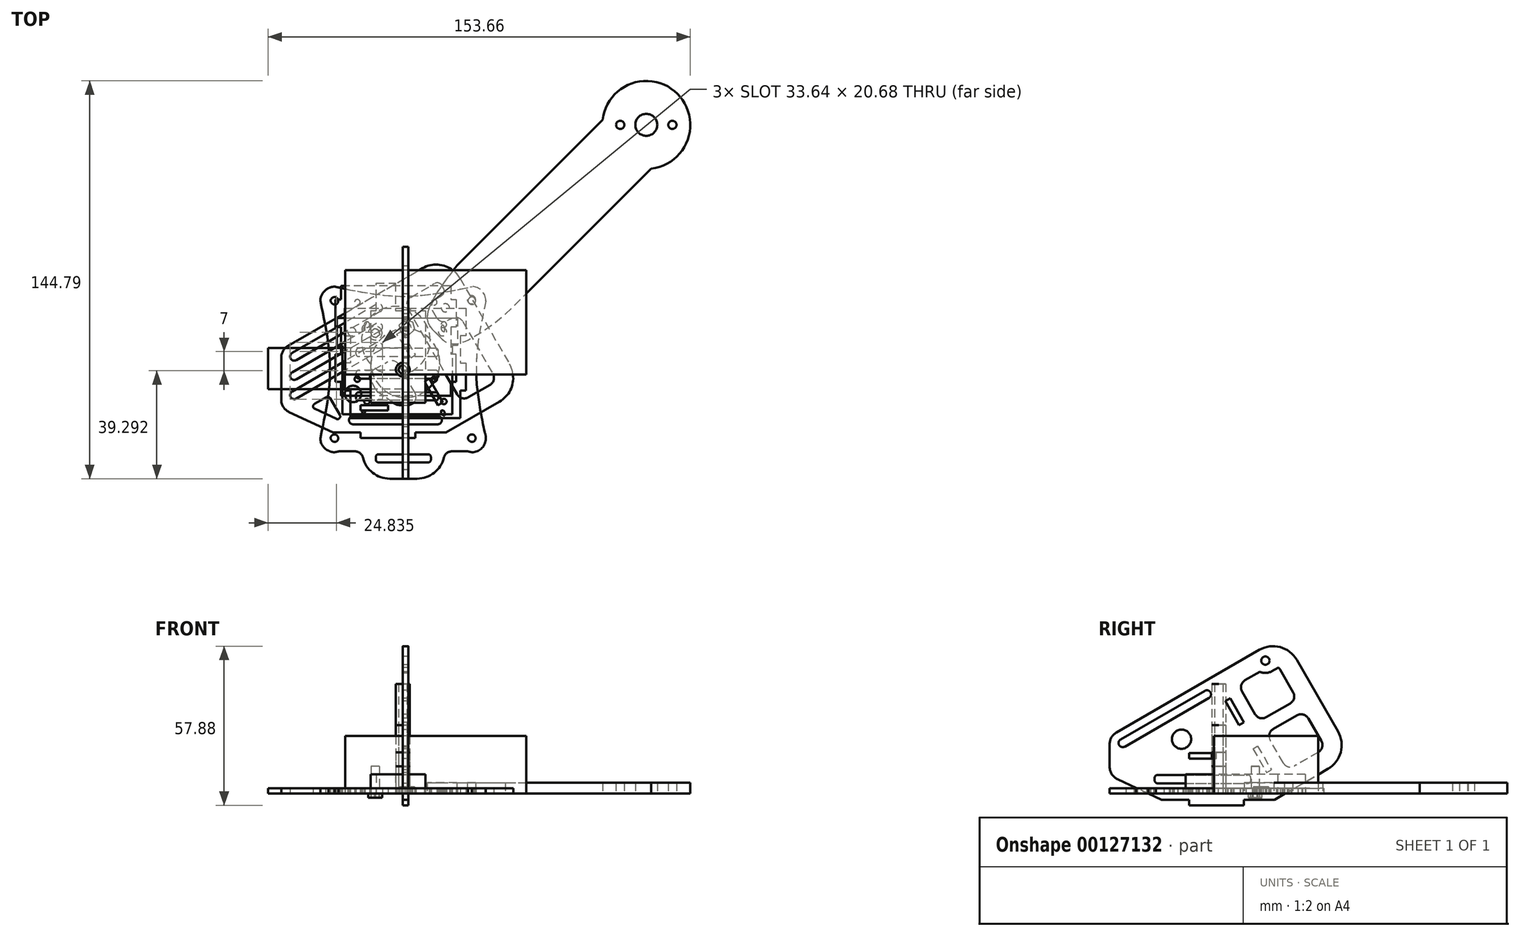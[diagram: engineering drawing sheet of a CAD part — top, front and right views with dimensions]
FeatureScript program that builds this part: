
annotation { "Feature Type Name" : "Feature", "Feature Type Description" : "" }
export const myFeature = defineFeature(function(context is Context, id is Id, definition is map)
    precondition{}
    {
        {
            var Q0;
            Q0=qCreatedBy(makeId("Top.planeOp"),FACE);
            var sketch = newSketch(context, id + "F0", { "sketchPlane" : qUnion([Q0])});
            skLineSegment(sketch, "E0.bottom", {"start": v(15.25, -15.25) * mm, "end": v(-15.25, -15.25) * mm, "construction": true});
            skLineSegment(sketch, "E0.top", {"start": v(15.25, 15.25) * mm, "end": v(-15.25, 15.25) * mm, "construction": true});
            skLineSegment(sketch, "E0.left", {"start": v(15.25, -15.25) * mm, "end": v(15.25, 15.25) * mm, "construction": true});
            skLineSegment(sketch, "E0.right", {"start": v(-15.25, -15.25) * mm, "end": v(-15.25, 15.25) * mm, "construction": true});
            skPoint(sketch, "E0.middle", {"position": v(0, 0) * mm});
            skCircle(sketch, "E1", {"center": v(-15.25, 15.25) * mm, "radius": 1.5 * mm});
            skCircle(sketch, "E2", {"center": v(15.25, 15.25) * mm, "radius": 1.5 * mm});
            skCircle(sketch, "E3", {"center": v(15.25, -15.25) * mm, "radius": 1.5 * mm});
            skCircle(sketch, "E4", {"center": v(-15.25, -15.25) * mm, "radius": 1.5 * mm});
            skLineSegment(sketch, "E5.bottom", {"start": v(18, -18) * mm, "end": v(-18, -18) * mm, "construction": true});
            skLineSegment(sketch, "E5.top", {"start": v(18, 18) * mm, "end": v(-18, 18) * mm, "construction": true});
            skLineSegment(sketch, "E5.left", {"start": v(18, -18) * mm, "end": v(18, 18) * mm, "construction": true});
            skLineSegment(sketch, "E5.right", {"start": v(-18, -18) * mm, "end": v(-18, 18) * mm, "construction": true});
            skLineSegment(sketch, "E6.bottom", {"start": v(25, -25) * mm, "end": v(-25, -25) * mm, "construction": true});
            skLineSegment(sketch, "E6.top", {"start": v(25, 25) * mm, "end": v(-25, 25) * mm, "construction": true});
            skLineSegment(sketch, "E6.left", {"start": v(25, -25) * mm, "end": v(25, 25) * mm, "construction": true});
            skLineSegment(sketch, "E6.right", {"start": v(-25, -25) * mm, "end": v(-25, 25) * mm, "construction": true});
            skCircle(sketch, "E7", {"center": v(-25, 25) * mm, "radius": 1.5 * mm});
            skCircle(sketch, "E8", {"center": v(25, 25) * mm, "radius": 1.5 * mm});
            skCircle(sketch, "E9", {"center": v(25, -25) * mm, "radius": 1.5 * mm});
            skCircle(sketch, "E10", {"center": v(-25, -25) * mm, "radius": 1.5 * mm});
            skLineSegment(sketch, "E11.bottom", {"start": v(12.5, -12.5) * mm, "end": v(-12.5, -12.5) * mm, "construction": true});
            skLineSegment(sketch, "E11.top", {"start": v(12.5, 12.5) * mm, "end": v(-12.5, 12.5) * mm, "construction": true});
            skLineSegment(sketch, "E11.left", {"start": v(12.5, -12.5) * mm, "end": v(12.5, 12.5) * mm, "construction": true});
            skLineSegment(sketch, "E11.right", {"start": v(-12.5, -12.5) * mm, "end": v(-12.5, 12.5) * mm, "construction": true});
            skArc(sketch, "E12", {"start": v(-15.25, 11.36) * mm, "mid": v(-12.5, 12.5) * mm, "end": v(-11.36, 15.25) * mm});
            skArc(sketch, "E13", {"start": v(15.25, -11.36) * mm, "mid": v(12.5, -12.5) * mm, "end": v(11.36, -15.25) * mm});
            skArc(sketch, "E14", {"start": v(-11.36, -15.25) * mm, "mid": v(-12.5, -12.5) * mm, "end": v(-15.25, -11.36) * mm});
            skLineSegment(sketch, "E15", {"start": v(-15.25, 11.36) * mm, "end": v(-15.25, -11.36) * mm});
            skLineSegment(sketch, "E16", {"start": v(-11.36, 15.25) * mm, "end": v(11.36, 15.25) * mm});
            skLineSegment(sketch, "E17", {"start": v(15.25, 11.36) * mm, "end": v(15.25, -11.36) * mm});
            skLineSegment(sketch, "E18", {"start": v(11.36, -15.25) * mm, "end": v(-11.36, -15.25) * mm});
            skArc(sketch, "E19.trimOffspring", {"start": v(11.36, 15.25) * mm, "mid": v(12.5, 12.5) * mm, "end": v(15.25, 11.36) * mm});
            skPoint(sketch, "E20.visualSharp", {"position": v(30, 30) * mm});
            skArc(sketch, "E20.filletArc", {"start": v(30, 25) * mm, "mid": v(28.54, 28.54) * mm, "end": v(25, 30) * mm});
            skPoint(sketch, "E21.visualSharp", {"position": v(-30, 30) * mm});
            skArc(sketch, "E21.filletArc", {"start": v(-25, 30) * mm, "mid": v(-28.54, 28.54) * mm, "end": v(-30, 25) * mm});
            skPoint(sketch, "E22.visualSharp", {"position": v(-30, -30) * mm});
            skArc(sketch, "E22.filletArc", {"start": v(-30, -25) * mm, "mid": v(-28.54, -28.54) * mm, "end": v(-25, -30) * mm});
            skPoint(sketch, "E23.visualSharp", {"position": v(30, -30) * mm});
            skArc(sketch, "E23.filletArc", {"start": v(25, -30) * mm, "mid": v(28.54, -28.54) * mm, "end": v(30, -25) * mm});
            skLineSegment(sketch, "E24", {"start": v(-26.5, 25) * mm, "end": v(-26.5, -25) * mm, "construction": true});
            skFitSpline(sketch, "E25", {"points": [v(-30, 25) * mm, v(-26.5, 0) * mm, v(-30, -25) * mm], "startDerivative": vector(10.5, -50) * mm, "endDerivative": vector(-10.5, -50) * mm});
            skLineSegment(sketch, "E26", {"start": v(-25, 26.5) * mm, "end": v(25, 26.5) * mm, "construction": true});
            skLineSegment(sketch, "E27", {"start": v(26.5, 25) * mm, "end": v(26.5, -25) * mm, "construction": true});
            skLineSegment(sketch, "E28", {"start": v(24.94, -26.5) * mm, "end": v(-25, -26.5) * mm, "construction": true});
            skFitSpline(sketch, "E29", {"points": [v(-25, 30) * mm, v(0, 26.5) * mm, v(25, 30) * mm], "startDerivative": vector(50, -10.5) * mm, "endDerivative": vector(50, 10.5) * mm});
            skFitSpline(sketch, "E30", {"points": [v(30, 25) * mm, v(26.5, 0) * mm, v(30, -25) * mm], "startDerivative": vector(-10.5, -50) * mm, "endDerivative": vector(10.5, -50) * mm});
            skPoint(sketch, "E31.1.internal.snap0", {"position": v(0, -25) * mm});
            skFitSpline(sketch, "E31", {"points": [v(-25, -30) * mm, v(0, -26.5) * mm, v(25, -30) * mm], "startDerivative": vector(50, 10.5) * mm, "endDerivative": vector(50, -10.5) * mm});
            skSolve(sketch);
        }
        {
            var Q0;
            Q0=makeQuery(id+"F0.imprint","IMPRINT",FACE,{"disambiguationData":[TD([[makeQuery(id+"F0.imprint","IMPRINT",EDGE,{"derivedFrom":sQuery(id+"F0.wireOp",EDGE,"E1")}),-1.0]])]});
            extrude(context, id + "F1", {"entities" : qUnion([Q0]), "depth" : 2 * mm});
        }
        {
            var Q0;
            Q0=qCreatedBy(makeId("Top.planeOp"),FACE);
            var sketch = newSketch(context, id + "F2", { "sketchPlane" : qUnion([Q0])});
            skCircle(sketch, "E32", {"center": v(0, 0) * mm, "radius": 2.5 * mm});
            skCircle(sketch, "E33", {"center": v(0, 0) * mm, "radius": 1.5 * mm});
            skSolve(sketch);
        }
        {
            var Q0;
            Q0 = qSketchRegion(id + "F2", true);
            extrude(context, id + "F3", {"entities" : qUnion([Q0]), "depth" : 25 * mm});
        }
        {
            var Q0;
            Q0=qCreatedBy(makeId("Top.planeOp"),FACE);
            var sketch = newSketch(context, id + "F4", { "sketchPlane" : qUnion([Q0])});
            skLineSegment(sketch, "E34.bottom", {"start": v(18, -18) * mm, "end": v(-18, -18) * mm});
            skLineSegment(sketch, "E34.top", {"start": v(18, 18) * mm, "end": v(-18, 18) * mm});
            skLineSegment(sketch, "E34.left", {"start": v(18, -18) * mm, "end": v(18, 18) * mm});
            skLineSegment(sketch, "E34.right", {"start": v(-18, -18) * mm, "end": v(-18, 18) * mm});
            skPoint(sketch, "E34.middle", {"position": v(0, 0) * mm});
            skLineSegment(sketch, "E35.bottom", {"start": v(-15.25, 15.25) * mm, "end": v(15.25, 15.25) * mm, "construction": true});
            skLineSegment(sketch, "E35.top", {"start": v(-15.25, -15.25) * mm, "end": v(15.25, -15.25) * mm, "construction": true});
            skLineSegment(sketch, "E35.left", {"start": v(-15.25, 15.25) * mm, "end": v(-15.25, -15.25) * mm, "construction": true});
            skLineSegment(sketch, "E35.right", {"start": v(15.25, 15.25) * mm, "end": v(15.25, -15.25) * mm, "construction": true});
            skCircle(sketch, "E36", {"center": v(-15.25, -15.25) * mm, "radius": 1.5 * mm});
            skCircle(sketch, "E37", {"center": v(-15.25, 15.25) * mm, "radius": 1.5 * mm});
            skCircle(sketch, "E38", {"center": v(15.25, 15.25) * mm, "radius": 1.5 * mm});
            skCircle(sketch, "E39", {"center": v(15.25, -15.25) * mm, "radius": 1.5 * mm});
            skSolve(sketch);
        }
        {
            var Q0;
            Q0 = qSketchRegion(id + "F4", true);
            extrude(context, id + "F5", {"entities" : qUnion([Q0]), "depth" : 2 * mm});
        }
        {
            var Q0;
            Q0=qCreatedBy(makeId("Top.planeOp"),FACE);
            var sketch = newSketch(context, id + "F6", { "sketchPlane" : qUnion([Q0])});
            skArc(sketch, "E40", {"start": v(16.31, 14.64) * mm, "mid": v(16.31, 16.76) * mm, "end": v(14.19, 16.76) * mm});
            skCircle(sketch, "E41", {"center": v(25, 25.45) * mm, "radius": 1.5 * mm});
            skPoint(sketch, "E42.visualSharp", {"position": v(30, 30.45) * mm});
            skLineSegment(sketch, "E43", {"start": v(15.25, 15.7) * mm, "end": v(25, 25.45) * mm, "construction": true});
            skLineSegment(sketch, "E44", {"start": v(28.54, 28.98) * mm, "end": v(88.64, 89.09) * mm, "construction": true});
            skCircle(sketch, "E45", {"center": v(88.64, 89.09) * mm, "radius": 13.75 * mm, "construction": true});
            skLineSegment(sketch, "E46.0", {"start": v(37.37, 20.14) * mm, "end": v(90.42, 73.18) * mm});
            skLineSegment(sketch, "E47.0", {"start": v(19.7, 37.82) * mm, "end": v(72.74, 90.86) * mm});
            skLineSegment(sketch, "E48", {"start": v(88.64, 89.09) * mm, "end": v(105.7, 106.14) * mm, "construction": true});
            skLineSegment(sketch, "E49", {"start": v(88.64, 89.09) * mm, "end": v(88.64, 75.34) * mm, "construction": true});
            skLineSegment(sketch, "E50", {"start": v(88.64, 89.09) * mm, "end": v(74.9, 89.09) * mm, "construction": true});
            skCircle(sketch, "E51", {"center": v(88.64, 89.09) * mm, "radius": 8 * mm, "construction": true});
            skCircle(sketch, "E52", {"center": v(88.64, 89.09) * mm, "radius": 9.5 * mm, "construction": true});
            skLineSegment(sketch, "E53", {"start": v(88.64, 89.09) * mm, "end": v(98.14, 89.09) * mm, "construction": true});
            skLineSegment(sketch, "E54", {"start": v(88.64, 89.09) * mm, "end": v(88.64, 98.59) * mm, "construction": true});
            skCircle(sketch, "E55", {"center": v(88.64, 81.09) * mm, "radius": 1.5 * mm, "construction": true});
            skCircle(sketch, "E56", {"center": v(79.14, 89.09) * mm, "radius": 1.5 * mm});
            skCircle(sketch, "E57", {"center": v(88.64, 97.09) * mm, "radius": 1.5 * mm, "construction": true});
            skCircle(sketch, "E58", {"center": v(98.14, 89.09) * mm, "radius": 1.5 * mm});
            skArc(sketch, "E59", {"start": v(90.42, 73.18) * mm, "mid": v(99.95, 100.4) * mm, "end": v(72.74, 90.86) * mm});
            skFitSpline(sketch, "E60", {"points": [v(19.7, 37.82) * mm, v(12.5, 12.95) * mm, v(37.37, 20.14) * mm], "startDerivative": vector(-93.64, -114.86) * mm, "endDerivative": vector(114.86, 93.64) * mm});
            skCircle(sketch, "E61", {"center": v(88.64, 89.09) * mm, "radius": 4 * mm});
            skLineSegment(sketch, "E62", {"start": v(11.16, 11.6) * mm, "end": v(21.63, 1.14) * mm, "construction": true});
            skLineSegment(sketch, "E63", {"start": v(11.16, 11.6) * mm, "end": v(-2.43, 25.2) * mm, "construction": true});
            skCircle(sketch, "E64", {"center": v(11.16, 11.6) * mm, "radius": 10 * mm, "construction": true});
            skLineSegment(sketch, "E65", {"start": v(15.25, 15.7) * mm, "end": v(18.25, 12.7) * mm, "construction": true});
            skLineSegment(sketch, "E66", {"start": v(15.25, 15.7) * mm, "end": v(12.88, 18.07) * mm, "construction": true});
            skLineSegment(sketch, "E67", {"start": v(14.19, 16.76) * mm, "end": v(11.42, 13.99) * mm});
            skLineSegment(sketch, "E68", {"start": v(16.31, 14.64) * mm, "end": v(13.54, 11.87) * mm});
            skFitSpline(sketch, "E69.trimOffspring", {"points": [v(19.7, 37.82) * mm, v(12.5, 12.95) * mm, v(37.37, 20.14) * mm], "startDerivative": vector(-93.64, -114.86) * mm, "endDerivative": vector(114.86, 93.64) * mm});
            skSolve(sketch);
        }
        {
            var Q0;
            Q0 = qSketchRegion(id + "F6", true);
            extrude(context, id + "F7", {"entities" : qUnion([Q0]), "depth" : 4 * mm});
        }
        {
            var Q0;
            Q0=qCreatedBy(makeId("Top.planeOp"),FACE);
            var sketch = newSketch(context, id + "F8", { "sketchPlane" : qUnion([Q0])});
            skPoint(sketch, "E70.visualSharp", {"position": v(30.19, 29.9) * mm});
            skArc(sketch, "E70.filletArc", {"start": v(30.19, 24.9) * mm, "mid": v(28.72, 28.44) * mm, "end": v(25.19, 29.9) * mm});
            skPoint(sketch, "E71.visualSharp", {"position": v(-29.81, 29.9) * mm});
            skArc(sketch, "E71.filletArc", {"start": v(-24.81, 29.9) * mm, "mid": v(-28.35, 28.44) * mm, "end": v(-29.81, 24.9) * mm});
            skPoint(sketch, "E72.visualSharp", {"position": v(-29.81, -30.1) * mm});
            skArc(sketch, "E72.filletArc", {"start": v(-29.81, -25.1) * mm, "mid": v(-28.35, -28.63) * mm, "end": v(-24.81, -30.1) * mm});
            skPoint(sketch, "E73.visualSharp", {"position": v(30.19, -30.1) * mm});
            skArc(sketch, "E73.filletArc", {"start": v(25.19, -30.1) * mm, "mid": v(28.72, -28.63) * mm, "end": v(30.19, -25.1) * mm});
            skFitSpline(sketch, "E74", {"points": [v(-29.81, 24.9) * mm, v(-26.31, -0.1) * mm, v(-29.81, -25.1) * mm], "startDerivative": vector(10.5, -50) * mm, "endDerivative": vector(-10.5, -50) * mm});
            skFitSpline(sketch, "E75", {"points": [v(-24.81, 29.9) * mm, v(0.19, 26.4) * mm, v(25.19, 29.9) * mm], "startDerivative": vector(50, -10.5) * mm, "endDerivative": vector(50, 10.5) * mm});
            skFitSpline(sketch, "E76", {"points": [v(30.19, 24.9) * mm, v(26.69, -0.1) * mm, v(30.19, -25.1) * mm], "startDerivative": vector(-10.5, -50) * mm, "endDerivative": vector(10.5, -50) * mm});
            skFitSpline(sketch, "E77", {"points": [v(-24.81, -30.1) * mm, v(0.19, -26.6) * mm, v(25.19, -30.1) * mm], "startDerivative": vector(50, 10.5) * mm, "endDerivative": vector(50, -10.5) * mm});
            skLineSegment(sketch, "E78", {"start": v(0.19, 26.4) * mm, "end": v(0.19, -26.6) * mm, "construction": true});
            skLineSegment(sketch, "E79", {"start": v(-26.31, -0.1) * mm, "end": v(26.69, -0.1) * mm, "construction": true});
            skCircle(sketch, "E80", {"center": v(-24.81, -25.1) * mm, "radius": 1.5 * mm});
            skCircle(sketch, "E81", {"center": v(25.19, -25.1) * mm, "radius": 1.5 * mm});
            skCircle(sketch, "E82", {"center": v(25.19, 24.9) * mm, "radius": 1.5 * mm});
            skCircle(sketch, "E83", {"center": v(-24.81, 24.9) * mm, "radius": 1.5 * mm});
            skLineSegment(sketch, "E84.left", {"start": v(17.7, -12.58) * mm, "end": v(17.68, 12.4) * mm, "construction": true});
            skPoint(sketch, "E84.middle", {"position": v(0.19, -0.1) * mm});
            skCircle(sketch, "E85", {"center": v(-15.06, 15.16) * mm, "radius": 1.5 * mm});
            skCircle(sketch, "E86", {"center": v(15.44, 15.16) * mm, "radius": 1.5 * mm});
            skCircle(sketch, "E87", {"center": v(15.44, -15.34) * mm, "radius": 1.5 * mm});
            skCircle(sketch, "E88", {"center": v(-15.06, -15.34) * mm, "radius": 1.5 * mm});
            skLineSegment(sketch, "E89.0", {"start": v(20.7, -12.58) * mm, "end": v(20.68, 12.4) * mm, "construction": true});
            skArc(sketch, "E90", {"start": v(20.68, 12.4) * mm, "mid": v(19.18, 13.9) * mm, "end": v(17.68, 12.4) * mm, "construction": true});
            skArc(sketch, "E91", {"start": v(17.7, -12.58) * mm, "mid": v(19.2, -14.08) * mm, "end": v(20.7, -12.58) * mm, "construction": true});
            skLineSegment(sketch, "E92.bottom", {"start": v(8.07, -10.1) * mm, "end": v(-7.7, -10.1) * mm});
            skLineSegment(sketch, "E92.top", {"start": v(8.07, 9.9) * mm, "end": v(-7.7, 9.9) * mm});
            skLineSegment(sketch, "E92.left", {"start": v(10.19, -7.97) * mm, "end": v(10.19, 7.79) * mm});
            skLineSegment(sketch, "E92.right", {"start": v(-9.81, -7.97) * mm, "end": v(-9.81, 7.79) * mm});
            skLineSegment(sketch, "E93", {"start": v(0.19, -0.1) * mm, "end": v(10.19, 9.9) * mm, "construction": true});
            skArc(sketch, "E94.MirrorCS", {"start": v(-12.31, -20.59) * mm, "mid": v(-13.81, -19.09) * mm, "end": v(-12.31, -17.59) * mm, "construction": true});
            skLineSegment(sketch, "E95.MirrorCS", {"start": v(-12.31, -20.59) * mm, "end": v(12.68, -20.6) * mm, "construction": true});
            skArc(sketch, "E96.MirrorCS", {"start": v(12.68, -17.6) * mm, "mid": v(14.18, -19.1) * mm, "end": v(12.68, -20.6) * mm, "construction": true});
            skLineSegment(sketch, "E97.MirrorCS", {"start": v(-12.31, -17.59) * mm, "end": v(12.68, -17.6) * mm, "construction": true});
            skArc(sketch, "E98.MirrorCS", {"start": v(-12.3, 17.41) * mm, "mid": v(-13.8, 18.91) * mm, "end": v(-12.3, 20.41) * mm, "construction": true});
            skLineSegment(sketch, "E99.MirrorCS", {"start": v(-12.3, 20.41) * mm, "end": v(12.7, 20.4) * mm, "construction": true});
            skLineSegment(sketch, "E100.MirrorCS", {"start": v(-12.3, 17.41) * mm, "end": v(12.69, 17.4) * mm, "construction": true});
            skArc(sketch, "E101.MirrorCS", {"start": v(12.7, 20.4) * mm, "mid": v(14.2, 18.9) * mm, "end": v(12.69, 17.4) * mm, "construction": true});
            skLineSegment(sketch, "E102.bottom", {"start": v(0.57, 2.4) * mm, "end": v(-0.2, 2.4) * mm});
            skLineSegment(sketch, "E102.top", {"start": v(0.57, -2.6) * mm, "end": v(-0.2, -2.6) * mm});
            skLineSegment(sketch, "E102.left", {"start": v(2.69, 0.29) * mm, "end": v(2.69, -0.47) * mm});
            skLineSegment(sketch, "E102.right", {"start": v(-2.31, 0.29) * mm, "end": v(-2.31, -0.47) * mm});
            skLineSegment(sketch, "E103.0", {"start": v(2.69, 0.29) * mm, "end": v(10.19, 7.79) * mm});
            skLineSegment(sketch, "E104.0", {"start": v(0.57, 2.4) * mm, "end": v(8.07, 9.9) * mm});
            skLineSegment(sketch, "E105.MirrorCS", {"start": v(0.57, -2.6) * mm, "end": v(8.07, -10.1) * mm});
            skLineSegment(sketch, "E106.MirrorCS", {"start": v(2.69, -0.47) * mm, "end": v(10.19, -7.97) * mm});
            skLineSegment(sketch, "E107.MirrorCS", {"start": v(-0.2, 2.4) * mm, "end": v(-7.7, 9.9) * mm});
            skLineSegment(sketch, "E108.MirrorCS", {"start": v(-2.31, 0.29) * mm, "end": v(-9.81, 7.79) * mm});
            skLineSegment(sketch, "E109.MirrorCS", {"start": v(-2.31, -0.47) * mm, "end": v(-9.81, -7.97) * mm});
            skLineSegment(sketch, "E110.MirrorCS", {"start": v(-0.2, -2.6) * mm, "end": v(-7.7, -10.1) * mm});
            skLineSegment(sketch, "E111", {"start": v(20.69, -0.1) * mm, "end": v(20.68, 9.9) * mm});
            skLineSegment(sketch, "E112", {"start": v(20.68, 9.9) * mm, "end": v(17.68, 9.9) * mm, "construction": true});
            skArc(sketch, "E113", {"start": v(20.69, 8.07) * mm, "mid": v(19.3, 9.9) * mm, "end": v(17.69, 8.28) * mm});
            skPoint(sketch, "E113.first.point", {"position": v(17.69, 8.5) * mm});
            skPoint(sketch, "E113.second.point", {"position": v(19.18, 9.9) * mm});
            skPoint(sketch, "E113.third.point", {"position": v(20.69, 8.07) * mm});
            skLineSegment(sketch, "E114.MirrorCS", {"start": v(20.68, -10.1) * mm, "end": v(17.68, -10.1) * mm, "construction": true});
            skArc(sketch, "E115.MirrorCS", {"start": v(20.69, -8.26) * mm, "mid": v(19.3, -10.09) * mm, "end": v(17.69, -8.47) * mm});
            skLineSegment(sketch, "E116", {"start": v(20.69, -0.1) * mm, "end": v(20.69, -8.26) * mm});
            skLineSegment(sketch, "E117", {"start": v(17.69, 8.28) * mm, "end": v(17.69, -8.47) * mm});
            skLineSegment(sketch, "E118.MirrorCS", {"start": v(-17.3, 8.28) * mm, "end": v(-17.3, -8.47) * mm});
            skLineSegment(sketch, "E119.MirrorCS", {"start": v(-20.31, -0.1) * mm, "end": v(-20.3, 9.9) * mm});
            skPoint(sketch, "E120.MirrorP", {"position": v(-20.3, 8.07) * mm});
            skLineSegment(sketch, "E121.MirrorCS", {"start": v(-17.32, -12.58) * mm, "end": v(-17.3, 12.4) * mm, "construction": true});
            skArc(sketch, "E122.MirrorCS", {"start": v(-20.3, 8.07) * mm, "mid": v(-18.93, 9.9) * mm, "end": v(-17.3, 8.28) * mm});
            skLineSegment(sketch, "E123.MirrorCS", {"start": v(-20.3, 9.9) * mm, "end": v(-17.3, 9.9) * mm, "construction": true});
            skPoint(sketch, "E124.MirrorP", {"position": v(-18.8, 9.9) * mm});
            skArc(sketch, "E125.MirrorCS", {"start": v(-20.3, 12.4) * mm, "mid": v(-18.8, 13.9) * mm, "end": v(-17.3, 12.4) * mm, "construction": true});
            skPoint(sketch, "E126.MirrorP", {"position": v(-17.3, 8.5) * mm});
            skLineSegment(sketch, "E127.MirrorCS", {"start": v(-20.32, -12.58) * mm, "end": v(-20.3, 12.4) * mm, "construction": true});
            skArc(sketch, "E128.MirrorCS", {"start": v(-17.32, -12.58) * mm, "mid": v(-18.82, -14.08) * mm, "end": v(-20.32, -12.58) * mm, "construction": true});
            skArc(sketch, "E129.MirrorCS", {"start": v(-20.3, -8.26) * mm, "mid": v(-18.93, -10.09) * mm, "end": v(-17.3, -8.47) * mm});
            skLineSegment(sketch, "E130.MirrorCS", {"start": v(-20.31, -0.1) * mm, "end": v(-20.3, -8.26) * mm});
            skLineSegment(sketch, "E131.MirrorCS", {"start": v(-20.3, -10.1) * mm, "end": v(-17.3, -10.1) * mm, "construction": true});
            skSolve(sketch);
        }
        {
            var Q0;
            Q0 = qSketchRegion(id + "F8", true);
            extrude(context, id + "F9", {"entities" : qUnion([Q0]), "depth" : 2 * mm});
        }
        {
            var Q0;
            Q0=qCreatedBy(makeId("Top.planeOp"),FACE);
            var sketch = newSketch(context, id + "F10", { "sketchPlane" : qUnion([Q0])});
            skPoint(sketch, "E132.visualSharp", {"position": v(30.23, 30.2) * mm});
            skArc(sketch, "E132.filletArc", {"start": v(30.23, 25.2) * mm, "mid": v(28.76, 28.73) * mm, "end": v(25.23, 30.2) * mm});
            skPoint(sketch, "E133.visualSharp", {"position": v(-29.77, 30.2) * mm});
            skArc(sketch, "E133.filletArc", {"start": v(-24.77, 30.2) * mm, "mid": v(-28.3, 28.73) * mm, "end": v(-29.77, 25.2) * mm});
            skPoint(sketch, "E134.visualSharp", {"position": v(-29.77, -29.8) * mm});
            skPoint(sketch, "E135.visualSharp", {"position": v(30.23, -29.8) * mm});
            skFitSpline(sketch, "E136", {"points": [v(-29.77, 25.2) * mm, v(-26.27, 0.2) * mm, v(-29.77, -24.8) * mm], "startDerivative": vector(10.5, -50) * mm, "endDerivative": vector(-10.5, -50) * mm});
            skFitSpline(sketch, "E137", {"points": [v(-24.77, 30.2) * mm, v(0.23, 26.7) * mm, v(25.23, 30.2) * mm], "startDerivative": vector(50, -10.5) * mm, "endDerivative": vector(50, 10.5) * mm});
            skFitSpline(sketch, "E138", {"points": [v(30.23, 25.2) * mm, v(26.73, 0.2) * mm, v(30.23, -24.8) * mm], "startDerivative": vector(-10.5, -50) * mm, "endDerivative": vector(10.5, -50) * mm});
            skCircle(sketch, "E139", {"center": v(-24.77, 25.2) * mm, "radius": 1.5 * mm});
            skCircle(sketch, "E140", {"center": v(25.23, 25.2) * mm, "radius": 1.5 * mm});
            skCircle(sketch, "E141", {"center": v(25.23, -24.8) * mm, "radius": 1.5 * mm});
            skCircle(sketch, "E142", {"center": v(-24.77, -24.8) * mm, "radius": 1.5 * mm});
            skLineSegment(sketch, "E143.top", {"start": v(5.23, -39.7) * mm, "end": v(-4.77, -39.7) * mm});
            skPoint(sketch, "E143.middle", {"position": v(0.23, -34.7) * mm});
            skArc(sketch, "E144.filletArc", {"start": v(-14.49, -32.06) * mm, "mid": v(-10.95, -37.56) * mm, "end": v(-4.77, -39.7) * mm});
            skLineSegment(sketch, "E145", {"start": v(-25.17, -29.79) * mm, "end": v(-17.4, -29.77) * mm});
            skArc(sketch, "E146.filletArc", {"start": v(-14.49, -32.06) * mm, "mid": v(-15.55, -30.41) * mm, "end": v(-17.4, -29.77) * mm});
            skArc(sketch, "E147", {"start": v(24.8, -29.79) * mm, "mid": v(29.3, -27.72) * mm, "end": v(29.8, -22.8) * mm});
            skArc(sketch, "E148", {"start": v(-29.35, -22.8) * mm, "mid": v(-28.84, -27.72) * mm, "end": v(-24.35, -29.79) * mm});
            skArc(sketch, "E149.MirrorCS", {"start": v(14.94, -32.06) * mm, "mid": v(11.4, -37.56) * mm, "end": v(5.23, -39.7) * mm});
            skLineSegment(sketch, "E150.MirrorCS", {"start": v(25.63, -29.79) * mm, "end": v(17.87, -29.77) * mm});
            skArc(sketch, "E151.MirrorCS", {"start": v(14.94, -32.06) * mm, "mid": v(16, -30.41) * mm, "end": v(17.87, -29.77) * mm});
            skLineSegment(sketch, "E152.left", {"start": v(20.23, -9.8) * mm, "end": v(20.23, 10.2) * mm});
            skLineSegment(sketch, "E152.right", {"start": v(-19.77, -9.8) * mm, "end": v(-19.77, 10.2) * mm});
            skPoint(sketch, "E152.middle", {"position": v(0.23, 0.2) * mm});
            skLineSegment(sketch, "E153.0", {"start": v(-21.77, -9.8) * mm, "end": v(-21.77, 10.2) * mm});
            skLineSegment(sketch, "E154.0", {"start": v(22.23, -9.8) * mm, "end": v(22.23, 10.2) * mm});
            skLineSegment(sketch, "E155", {"start": v(-21.77, 10.2) * mm, "end": v(-19.77, 10.2) * mm});
            skLineSegment(sketch, "E156", {"start": v(20.23, 10.2) * mm, "end": v(22.23, 10.2) * mm});
            skLineSegment(sketch, "E157", {"start": v(22.23, -9.8) * mm, "end": v(20.23, -9.8) * mm});
            skLineSegment(sketch, "E158", {"start": v(-19.77, -9.8) * mm, "end": v(-21.77, -9.8) * mm});
            skLineSegment(sketch, "E159", {"start": v(-19.77, -9.8) * mm, "end": v(-19.77, -4.8) * mm, "construction": true});
            skLineSegment(sketch, "E160", {"start": v(20.23, -4.8) * mm, "end": v(16.73, -4.8) * mm, "construction": true});
            skCircle(sketch, "E161", {"center": v(16.73, -4.8) * mm, "radius": 1.5 * mm});
            skCircle(sketch, "E162.MirrorC", {"center": v(-16.27, -4.8) * mm, "radius": 1.5 * mm});
            skLineSegment(sketch, "E163", {"start": v(-19.77, -4.8) * mm, "end": v(16.73, -4.8) * mm, "construction": true});
            skLineSegment(sketch, "E164.bottom", {"start": v(5.73, -9.8) * mm, "end": v(-5.27, -9.8) * mm});
            skLineSegment(sketch, "E164.top", {"start": v(5.73, 0.2) * mm, "end": v(-5.27, 0.2) * mm});
            skLineSegment(sketch, "E164.left", {"start": v(7.73, -7.8) * mm, "end": v(7.73, -1.8) * mm});
            skLineSegment(sketch, "E164.right", {"start": v(-7.27, -7.8) * mm, "end": v(-7.27, -1.8) * mm});
            skPoint(sketch, "E164.middle", {"position": v(0.23, -4.8) * mm});
            skPoint(sketch, "E165.visualSharp", {"position": v(-7.27, -9.8) * mm});
            skArc(sketch, "E165.filletArc", {"start": v(-7.27, -7.8) * mm, "mid": v(-6.69, -9.22) * mm, "end": v(-5.27, -9.8) * mm});
            skPoint(sketch, "E166.visualSharp", {"position": v(7.73, -9.8) * mm});
            skArc(sketch, "E166.filletArc", {"start": v(5.73, -9.8) * mm, "mid": v(7.14, -9.22) * mm, "end": v(7.73, -7.8) * mm});
            skPoint(sketch, "E167.visualSharp", {"position": v(7.73, 0.2) * mm});
            skArc(sketch, "E167.filletArc", {"start": v(7.73, -1.8) * mm, "mid": v(7.14, -0.4) * mm, "end": v(5.73, 0.2) * mm});
            skPoint(sketch, "E168.visualSharp", {"position": v(-7.27, 0.2) * mm});
            skArc(sketch, "E168.filletArc", {"start": v(-5.27, 0.2) * mm, "mid": v(-6.69, -0.4) * mm, "end": v(-7.27, -1.8) * mm});
            skLineSegment(sketch, "E169", {"start": v(0.23, 0.2) * mm, "end": v(0.23, 5.2) * mm, "construction": true});
            skLineSegment(sketch, "E170", {"start": v(0.23, 5.2) * mm, "end": v(0.23, 8.2) * mm, "construction": true});
            skLineSegment(sketch, "E171", {"start": v(0.23, 8.2) * mm, "end": v(0.23, 13.2) * mm, "construction": true});
            skLineSegment(sketch, "E172", {"start": v(0.23, 13.2) * mm, "end": v(0.23, 16.2) * mm, "construction": true});
            skLineSegment(sketch, "E173", {"start": v(0.23, -9.8) * mm, "end": v(0.23, -14.8) * mm, "construction": true});
            skLineSegment(sketch, "E174", {"start": v(0.23, -14.8) * mm, "end": v(0.23, -17.8) * mm, "construction": true});
            skLineSegment(sketch, "E175", {"start": v(0.23, -17.8) * mm, "end": v(0.23, -22.8) * mm, "construction": true});
            skLineSegment(sketch, "E176", {"start": v(0.23, -22.8) * mm, "end": v(0.23, -25.8) * mm, "construction": true});
            skLineSegment(sketch, "E177.bottom", {"start": v(14.23, -17.8) * mm, "end": v(-13.77, -17.8) * mm});
            skLineSegment(sketch, "E177.top", {"start": v(14.23, -14.8) * mm, "end": v(-13.77, -14.8) * mm});
            skLineSegment(sketch, "E177.left", {"start": v(15.23, -16.8) * mm, "end": v(15.23, -15.8) * mm});
            skLineSegment(sketch, "E177.right", {"start": v(-14.77, -16.8) * mm, "end": v(-14.77, -15.8) * mm});
            skPoint(sketch, "E177.middle", {"position": v(0.23, -16.3) * mm});
            skLineSegment(sketch, "E178.bottom", {"start": v(14.23, -25.8) * mm, "end": v(-13.77, -25.8) * mm});
            skLineSegment(sketch, "E178.top", {"start": v(14.23, -22.8) * mm, "end": v(-13.77, -22.8) * mm});
            skLineSegment(sketch, "E178.left", {"start": v(15.23, -24.8) * mm, "end": v(15.23, -23.8) * mm});
            skLineSegment(sketch, "E178.right", {"start": v(-14.77, -24.8) * mm, "end": v(-14.77, -23.8) * mm});
            skPoint(sketch, "E178.middle", {"position": v(0.23, -24.3) * mm});
            skLineSegment(sketch, "E179.bottom", {"start": v(14.23, 5.2) * mm, "end": v(-13.77, 5.2) * mm});
            skLineSegment(sketch, "E179.top", {"start": v(14.23, 8.2) * mm, "end": v(-13.77, 8.2) * mm});
            skLineSegment(sketch, "E179.left", {"start": v(15.23, 6.2) * mm, "end": v(15.23, 7.2) * mm});
            skLineSegment(sketch, "E179.right", {"start": v(-14.77, 6.2) * mm, "end": v(-14.77, 7.2) * mm});
            skPoint(sketch, "E179.middle", {"position": v(0.23, 6.7) * mm});
            skLineSegment(sketch, "E180.bottom", {"start": v(14.23, 13.2) * mm, "end": v(-13.77, 13.2) * mm});
            skLineSegment(sketch, "E180.top", {"start": v(14.23, 16.2) * mm, "end": v(-13.77, 16.2) * mm});
            skLineSegment(sketch, "E180.left", {"start": v(15.23, 14.2) * mm, "end": v(15.23, 15.2) * mm});
            skLineSegment(sketch, "E180.right", {"start": v(-14.77, 14.2) * mm, "end": v(-14.77, 15.2) * mm});
            skPoint(sketch, "E180.middle", {"position": v(0.23, 14.7) * mm});
            skPoint(sketch, "E181.visualSharp", {"position": v(-14.77, -25.8) * mm});
            skArc(sketch, "E181.filletArc", {"start": v(-14.77, -24.8) * mm, "mid": v(-14.48, -25.51) * mm, "end": v(-13.77, -25.8) * mm});
            skPoint(sketch, "E182.visualSharp", {"position": v(-14.77, -22.8) * mm});
            skArc(sketch, "E182.filletArc", {"start": v(-13.77, -22.8) * mm, "mid": v(-14.48, -23.1) * mm, "end": v(-14.77, -23.8) * mm});
            skPoint(sketch, "E183.visualSharp", {"position": v(15.23, -22.8) * mm});
            skArc(sketch, "E183.filletArc", {"start": v(15.23, -23.8) * mm, "mid": v(14.94, -23.1) * mm, "end": v(14.23, -22.8) * mm});
            skPoint(sketch, "E184.visualSharp", {"position": v(15.23, -25.8) * mm});
            skArc(sketch, "E184.filletArc", {"start": v(14.23, -25.8) * mm, "mid": v(14.94, -25.51) * mm, "end": v(15.23, -24.8) * mm});
            skPoint(sketch, "E185.visualSharp", {"position": v(-14.77, -14.8) * mm});
            skArc(sketch, "E185.filletArc", {"start": v(-13.77, -14.8) * mm, "mid": v(-14.48, -15.1) * mm, "end": v(-14.77, -15.8) * mm});
            skPoint(sketch, "E186.visualSharp", {"position": v(-14.77, -17.8) * mm});
            skArc(sketch, "E186.filletArc", {"start": v(-14.77, -16.8) * mm, "mid": v(-14.48, -17.51) * mm, "end": v(-13.77, -17.8) * mm});
            skPoint(sketch, "E187.visualSharp", {"position": v(15.23, -14.8) * mm});
            skArc(sketch, "E187.filletArc", {"start": v(15.23, -15.8) * mm, "mid": v(14.94, -15.1) * mm, "end": v(14.23, -14.8) * mm});
            skPoint(sketch, "E188.visualSharp", {"position": v(15.23, -17.8) * mm});
            skArc(sketch, "E188.filletArc", {"start": v(14.23, -17.8) * mm, "mid": v(14.94, -17.51) * mm, "end": v(15.23, -16.8) * mm});
            skPoint(sketch, "E189.visualSharp", {"position": v(15.23, 5.2) * mm});
            skArc(sketch, "E189.filletArc", {"start": v(14.23, 5.2) * mm, "mid": v(14.94, 5.49) * mm, "end": v(15.23, 6.2) * mm});
            skPoint(sketch, "E190.visualSharp", {"position": v(15.23, 8.2) * mm});
            skArc(sketch, "E190.filletArc", {"start": v(15.23, 7.2) * mm, "mid": v(14.94, 7.9) * mm, "end": v(14.23, 8.2) * mm});
            skPoint(sketch, "E191.visualSharp", {"position": v(-14.77, 8.2) * mm});
            skArc(sketch, "E191.filletArc", {"start": v(-13.77, 8.2) * mm, "mid": v(-14.48, 7.9) * mm, "end": v(-14.77, 7.2) * mm});
            skPoint(sketch, "E192.visualSharp", {"position": v(-14.77, 5.2) * mm});
            skArc(sketch, "E192.filletArc", {"start": v(-14.77, 6.2) * mm, "mid": v(-14.48, 5.49) * mm, "end": v(-13.77, 5.2) * mm});
            skPoint(sketch, "E193.visualSharp", {"position": v(-14.77, 16.2) * mm});
            skArc(sketch, "E193.filletArc", {"start": v(-13.77, 16.2) * mm, "mid": v(-14.48, 15.9) * mm, "end": v(-14.77, 15.2) * mm});
            skPoint(sketch, "E194.visualSharp", {"position": v(15.23, 16.2) * mm});
            skArc(sketch, "E194.filletArc", {"start": v(15.23, 15.2) * mm, "mid": v(14.94, 15.9) * mm, "end": v(14.23, 16.2) * mm});
            skPoint(sketch, "E195.visualSharp", {"position": v(15.23, 13.2) * mm});
            skArc(sketch, "E195.filletArc", {"start": v(14.23, 13.2) * mm, "mid": v(14.94, 13.49) * mm, "end": v(15.23, 14.2) * mm});
            skPoint(sketch, "E196.visualSharp", {"position": v(-14.77, 13.2) * mm});
            skArc(sketch, "E196.filletArc", {"start": v(-14.77, 14.2) * mm, "mid": v(-14.48, 13.49) * mm, "end": v(-13.77, 13.2) * mm});
            skLineSegment(sketch, "E197", {"start": v(0.23, 16.2) * mm, "end": v(0.23, 21.2) * mm, "construction": true});
            skLineSegment(sketch, "E198", {"start": v(0.23, 21.2) * mm, "end": v(0.23, 24.2) * mm, "construction": true});
            skLineSegment(sketch, "E199.bottom", {"start": v(14.23, 21.2) * mm, "end": v(-13.77, 21.2) * mm});
            skLineSegment(sketch, "E199.top", {"start": v(14.23, 24.2) * mm, "end": v(-13.77, 24.2) * mm});
            skLineSegment(sketch, "E199.left", {"start": v(15.23, 22.2) * mm, "end": v(15.23, 23.2) * mm});
            skLineSegment(sketch, "E199.right", {"start": v(-14.77, 22.2) * mm, "end": v(-14.77, 23.2) * mm});
            skPoint(sketch, "E199.middle", {"position": v(0.23, 22.7) * mm});
            skPoint(sketch, "E200.visualSharp", {"position": v(-14.77, 24.2) * mm});
            skArc(sketch, "E200.filletArc", {"start": v(-13.77, 24.2) * mm, "mid": v(-14.48, 23.9) * mm, "end": v(-14.77, 23.2) * mm});
            skPoint(sketch, "E201.visualSharp", {"position": v(-14.77, 21.2) * mm});
            skArc(sketch, "E201.filletArc", {"start": v(-14.77, 22.2) * mm, "mid": v(-14.48, 21.49) * mm, "end": v(-13.77, 21.2) * mm});
            skPoint(sketch, "E202.visualSharp", {"position": v(15.23, 21.2) * mm});
            skArc(sketch, "E202.filletArc", {"start": v(14.23, 21.2) * mm, "mid": v(14.94, 21.49) * mm, "end": v(15.23, 22.2) * mm});
            skPoint(sketch, "E203.visualSharp", {"position": v(15.23, 24.2) * mm});
            skArc(sketch, "E203.filletArc", {"start": v(15.23, 23.2) * mm, "mid": v(14.94, 23.9) * mm, "end": v(14.23, 24.2) * mm});
            skLineSegment(sketch, "E204", {"start": v(0.23, -25.8) * mm, "end": v(0.23, -30.8) * mm, "construction": true});
            skLineSegment(sketch, "E205", {"start": v(0.23, -30.8) * mm, "end": v(0.23, -33.8) * mm, "construction": true});
            skLineSegment(sketch, "E206.bottom", {"start": v(9.23, -33.8) * mm, "end": v(-8.77, -33.8) * mm});
            skLineSegment(sketch, "E206.top", {"start": v(9.23, -30.8) * mm, "end": v(-8.77, -30.8) * mm});
            skLineSegment(sketch, "E206.left", {"start": v(10.23, -32.8) * mm, "end": v(10.23, -31.8) * mm});
            skLineSegment(sketch, "E206.right", {"start": v(-9.77, -32.8) * mm, "end": v(-9.77, -31.8) * mm});
            skPoint(sketch, "E206.middle", {"position": v(0.23, -32.3) * mm});
            skPoint(sketch, "E207.visualSharp", {"position": v(10.23, -30.8) * mm});
            skArc(sketch, "E207.filletArc", {"start": v(10.23, -31.8) * mm, "mid": v(9.94, -31.1) * mm, "end": v(9.23, -30.8) * mm});
            skPoint(sketch, "E208.visualSharp", {"position": v(10.23, -33.8) * mm});
            skArc(sketch, "E208.filletArc", {"start": v(9.23, -33.8) * mm, "mid": v(9.94, -33.51) * mm, "end": v(10.23, -32.8) * mm});
            skPoint(sketch, "E209.visualSharp", {"position": v(-9.77, -30.8) * mm});
            skArc(sketch, "E209.filletArc", {"start": v(-8.77, -30.8) * mm, "mid": v(-9.48, -31.1) * mm, "end": v(-9.77, -31.8) * mm});
            skPoint(sketch, "E210.visualSharp", {"position": v(-9.77, -33.8) * mm});
            skArc(sketch, "E210.filletArc", {"start": v(-9.77, -32.8) * mm, "mid": v(-9.48, -33.51) * mm, "end": v(-8.77, -33.8) * mm});
            skSolve(sketch);
        }
        {
            var Q0;
            Q0=qCreatedBy(makeId("Top.planeOp"),FACE);
            var sketch = newSketch(context, id + "F11", { "sketchPlane" : qUnion([Q0])});
            skCircle(sketch, "E211", {"center": v(1.48, 15.4) * mm, "radius": 1.5 * mm});
            skLineSegment(sketch, "E212.0", {"start": v(4.25, 14.6) * mm, "end": v(2.16, 12.6) * mm});
            skLineSegment(sketch, "E212.1", {"start": v(2.16, 12.6) * mm, "end": v(-0.6, 13.4) * mm});
            skLineSegment(sketch, "E212.2", {"start": v(-0.6, 13.4) * mm, "end": v(-1.3, 16.21) * mm});
            skLineSegment(sketch, "E212.3", {"start": v(-1.3, 16.21) * mm, "end": v(0.8, 18.2) * mm});
            skLineSegment(sketch, "E212.4", {"start": v(0.8, 18.2) * mm, "end": v(3.56, 17.4) * mm});
            skLineSegment(sketch, "E212.5", {"start": v(3.56, 17.4) * mm, "end": v(4.25, 14.6) * mm});
            skPoint(sketch, "E212.0.midPoint", {"position": v(3.2, 13.6) * mm});
            skSolve(sketch);
        }
        {
            var Q0;
            Q0 = qSketchRegion(id + "F11", true);
            extrude(context, id + "F12", {"entities" : qUnion([Q0]), "depth" : 2.5 * mm});
        }
        {
            var Q0;
            Q0 = qSketchRegion(id + "F2", true);
            extrude(context, id + "F13", {"entities" : qUnion([Q0]), "depth" : 10 * mm});
        }
        {
            var Q0;
            Q0 = qSketchRegion(id + "F10", true);
            extrude(context, id + "F14", {"entities" : qUnion([Q0]), "depth" : 2 * mm});
        }
        {
            var Q0;
            Q0=qCreatedBy(makeId("Top.planeOp"),FACE);
            var sketch = newSketch(context, id + "F15", { "sketchPlane" : qUnion([Q0])});
            skCircle(sketch, "E213", {"center": v(-10.03, 13.3) * mm, "radius": 1.5 * mm});
            skCircle(sketch, "E214", {"center": v(-10.03, 13.3) * mm, "radius": 2.5 * mm});
            skCircle(sketch, "E215.cCircle", {"center": v(-10.03, 13.3) * mm, "radius": 1.5 * mm, "construction": true});
            skLineSegment(sketch, "E215.0", {"start": v(-10.26, 15.02) * mm, "end": v(-8.66, 14.36) * mm});
            skLineSegment(sketch, "E215.1", {"start": v(-8.66, 14.36) * mm, "end": v(-8.43, 12.64) * mm});
            skLineSegment(sketch, "E215.2", {"start": v(-8.43, 12.64) * mm, "end": v(-9.8, 11.58) * mm});
            skLineSegment(sketch, "E215.3", {"start": v(-9.8, 11.58) * mm, "end": v(-11.4, 12.25) * mm});
            skLineSegment(sketch, "E215.4", {"start": v(-11.4, 12.25) * mm, "end": v(-11.63, 13.97) * mm});
            skLineSegment(sketch, "E215.5", {"start": v(-11.63, 13.97) * mm, "end": v(-10.26, 15.02) * mm});
            skPoint(sketch, "E215.0.midPoint", {"position": v(-9.46, 14.69) * mm});
            skCircle(sketch, "E216", {"center": v(-10.03, 13.3) * mm, "radius": 1.73 * mm});
            skSolve(sketch);
        }
        {
            var Q0;
            {var subQ1=sQuery(id+"F15.wireOp",EDGE,"E215.0");var subQ3=makeQuery(id+"F15.imprint","INTERSECT",VERTEX,{"derivedFrom":[sQuery(id+"F15.wireOp",EDGE,"E213"),subQ1]});Q0=makeQuery(id+"F15.imprint","IMPRINT",FACE,{"disambiguationData":[TD([[makeQuery(id+"F15.imprint","IMPRINT",EDGE,{"disambiguationData":[TD([[subQ3,1.0]])],"derivedFrom":subQ1}),1.0]])]});}
            var Q1;
            {var subQ1=sQuery(id+"F15.wireOp",EDGE,"E215.5");var subQ3=makeQuery(id+"F15.imprint","INTERSECT",VERTEX,{"derivedFrom":[sQuery(id+"F15.wireOp",EDGE,"E213"),subQ1]});Q1=makeQuery(id+"F15.imprint","IMPRINT",FACE,{"disambiguationData":[TD([[makeQuery(id+"F15.imprint","IMPRINT",EDGE,{"disambiguationData":[TD([[subQ3,1.0]])],"derivedFrom":subQ1}),1.0]])]});}
            var Q2;
            {var subQ1=sQuery(id+"F15.wireOp",EDGE,"E215.4");var subQ3=makeQuery(id+"F15.imprint","INTERSECT",VERTEX,{"derivedFrom":[sQuery(id+"F15.wireOp",EDGE,"E213"),subQ1]});Q2=makeQuery(id+"F15.imprint","IMPRINT",FACE,{"disambiguationData":[TD([[makeQuery(id+"F15.imprint","IMPRINT",EDGE,{"disambiguationData":[TD([[subQ3,1.0]])],"derivedFrom":subQ1}),1.0]])]});}
            var Q3;
            {var subQ1=sQuery(id+"F15.wireOp",EDGE,"E215.3");var subQ3=makeQuery(id+"F15.imprint","INTERSECT",VERTEX,{"derivedFrom":[sQuery(id+"F15.wireOp",EDGE,"E213"),subQ1]});Q3=makeQuery(id+"F15.imprint","IMPRINT",FACE,{"disambiguationData":[TD([[makeQuery(id+"F15.imprint","IMPRINT",EDGE,{"disambiguationData":[TD([[subQ3,1.0]])],"derivedFrom":subQ1}),1.0]])]});}
            var Q4;
            {var subQ1=sQuery(id+"F15.wireOp",EDGE,"E215.2");var subQ3=makeQuery(id+"F15.imprint","INTERSECT",VERTEX,{"derivedFrom":[sQuery(id+"F15.wireOp",EDGE,"E213"),subQ1]});Q4=makeQuery(id+"F15.imprint","IMPRINT",FACE,{"disambiguationData":[TD([[makeQuery(id+"F15.imprint","IMPRINT",EDGE,{"disambiguationData":[TD([[subQ3,1.0]])],"derivedFrom":subQ1}),1.0]])]});}
            var Q5;
            {var subQ1=sQuery(id+"F15.wireOp",EDGE,"E215.1");var subQ3=makeQuery(id+"F15.imprint","INTERSECT",VERTEX,{"derivedFrom":[sQuery(id+"F15.wireOp",EDGE,"E213"),subQ1]});Q5=makeQuery(id+"F15.imprint","IMPRINT",FACE,{"disambiguationData":[TD([[makeQuery(id+"F15.imprint","IMPRINT",EDGE,{"disambiguationData":[TD([[subQ3,1.0]])],"derivedFrom":subQ1}),1.0]])]});}
            var Q6;
            Q6=makeQuery(id+"F15.imprint","IMPRINT",FACE,{"disambiguationData":[TD([[makeQuery(id+"F15.imprint","IMPRINT",EDGE,{"derivedFrom":sQuery(id+"F15.wireOp",EDGE,"E214")}),1.0]])]});
            extrude(context, id + "F16", {"entities" : qUnion([Q0, Q1, Q2, Q3, Q4, Q5, Q6]), "oppositeDirection" : true, "depth" : 3 * mm, "symmetric" : true});
        }
        {
            var Q0;
            {var subQ0=sQuery(id+"F15.wireOp",EDGE,"E215.3");var subQ1=sQuery(id+"F15.wireOp",EDGE,"E213");var subQ2=makeQuery(id+"F15.imprint","INTERSECT",VERTEX,{"derivedFrom":[subQ1,subQ0]});Q0=makeQuery(id+"F15.imprint","IMPRINT",FACE,{"disambiguationData":[TD([[makeQuery(id+"F15.imprint","IMPRINT",EDGE,{"disambiguationData":[TD([[subQ2,-1.0]])],"derivedFrom":subQ1}),-1.0]])]});}
            var Q1;
            {var subQ0=sQuery(id+"F15.wireOp",EDGE,"E215.1");var subQ1=sQuery(id+"F15.wireOp",EDGE,"E213");var subQ2=makeQuery(id+"F15.imprint","INTERSECT",VERTEX,{"derivedFrom":[subQ1,subQ0]});Q1=makeQuery(id+"F15.imprint","IMPRINT",FACE,{"disambiguationData":[TD([[makeQuery(id+"F15.imprint","IMPRINT",EDGE,{"disambiguationData":[TD([[subQ2,1.0]])],"derivedFrom":subQ1}),-1.0]])]});}
            var Q2;
            {var subQ0=sQuery(id+"F15.wireOp",EDGE,"E215.0");var subQ1=sQuery(id+"F15.wireOp",EDGE,"E213");var subQ2=makeQuery(id+"F15.imprint","INTERSECT",VERTEX,{"derivedFrom":[subQ1,subQ0]});Q2=makeQuery(id+"F15.imprint","IMPRINT",FACE,{"disambiguationData":[TD([[makeQuery(id+"F15.imprint","IMPRINT",EDGE,{"disambiguationData":[TD([[subQ2,1.0]])],"derivedFrom":subQ1}),-1.0]])]});}
            var Q3;
            {var subQ0=sQuery(id+"F15.wireOp",EDGE,"E215.0");var subQ1=sQuery(id+"F15.wireOp",EDGE,"E213");var subQ2=makeQuery(id+"F15.imprint","INTERSECT",VERTEX,{"derivedFrom":[subQ1,subQ0]});Q3=makeQuery(id+"F15.imprint","IMPRINT",FACE,{"disambiguationData":[TD([[makeQuery(id+"F15.imprint","IMPRINT",EDGE,{"disambiguationData":[TD([[subQ2,-1.0]])],"derivedFrom":subQ1}),-1.0]])]});}
            var Q4;
            {var subQ0=sQuery(id+"F15.wireOp",EDGE,"E215.5");var subQ1=sQuery(id+"F15.wireOp",EDGE,"E213");var subQ2=makeQuery(id+"F15.imprint","INTERSECT",VERTEX,{"derivedFrom":[subQ1,subQ0]});Q4=makeQuery(id+"F15.imprint","IMPRINT",FACE,{"disambiguationData":[TD([[makeQuery(id+"F15.imprint","IMPRINT",EDGE,{"disambiguationData":[TD([[subQ2,-1.0]])],"derivedFrom":subQ1}),-1.0]])]});}
            var Q5;
            {var subQ0=sQuery(id+"F15.wireOp",EDGE,"E215.4");var subQ1=sQuery(id+"F15.wireOp",EDGE,"E213");var subQ2=makeQuery(id+"F15.imprint","INTERSECT",VERTEX,{"derivedFrom":[subQ1,subQ0]});Q5=makeQuery(id+"F15.imprint","IMPRINT",FACE,{"disambiguationData":[TD([[makeQuery(id+"F15.imprint","IMPRINT",EDGE,{"disambiguationData":[TD([[subQ2,-1.0]])],"derivedFrom":subQ1}),-1.0]])]});}
            extrude(context, id + "F17", {"entities" : qUnion([Q0, Q1, Q2, Q3, Q4, Q5]), "operationType" : NewBodyOperationType.ADD, "depth" : 1.5 * mm});
        }
        {
            var Q0;
            {var subQ0=sQuery(id+"F15.wireOp",EDGE,"E213");var subQ4=makeQuery(id+"F15.imprint","INTERSECT",VERTEX,{"derivedFrom":[subQ0,sQuery(id+"F15.wireOp",EDGE,"E215.0")]});Q0=makeQuery(id+"F15.imprint","IMPRINT",FACE,{"disambiguationData":[TD([[makeQuery(id+"F15.imprint","IMPRINT",EDGE,{"disambiguationData":[TD([[subQ4,1.0]])],"derivedFrom":subQ0}),1.0]])]});}
            extrude(context, id + "F18", {"entities" : qUnion([Q0]), "operationType" : NewBodyOperationType.ADD, "depth" : 10 * mm});
        }
        {
            var Q0;
            Q0=qCreatedBy(makeId("Right.planeOp"),FACE);
            var sketch = newSketch(context, id + "F19", { "sketchPlane" : qUnion([Q0])});
            skLineSegment(sketch, "E217.bottom", {"start": v(-20.84, -2.21) * mm, "end": v(-10.82, -2.21) * mm});
            skLineSegment(sketch, "E218.top", {"start": v(9.18, -4.21) * mm, "end": v(-10.82, -4.21) * mm});
            skLineSegment(sketch, "E218.left", {"start": v(9.18, -2.21) * mm, "end": v(9.18, -4.21) * mm});
            skLineSegment(sketch, "E218.right", {"start": v(-10.82, -2.21) * mm, "end": v(-10.82, -4.21) * mm});
            skLineSegment(sketch, "E219.trimOffspring", {"start": v(9.18, -2.21) * mm, "end": v(20.29, -2.21) * mm});
            skLineSegment(sketch, "E220", {"start": v(20.29, -2.21) * mm, "end": v(39.76, 9.03) * mm});
            skLineSegment(sketch, "E221", {"start": v(-20.84, -2.21) * mm, "end": v(-36.82, 5.24) * mm});
            skLineSegment(sketch, "E222", {"start": v(-39.7, 18) * mm, "end": v(-39.7, 9.77) * mm});
            skPoint(sketch, "E223.visualSharp", {"position": v(-39.7, 20.89) * mm});
            skArc(sketch, "E223.filletArc", {"start": v(-37.2, 22.33) * mm, "mid": v(-39.03, 20.5) * mm, "end": v(-39.7, 18) * mm});
            skPoint(sketch, "E224.visualSharp", {"position": v(-39.7, 6.59) * mm});
            skArc(sketch, "E224.filletArc", {"start": v(-39.7, 9.77) * mm, "mid": v(-38.92, 7.08) * mm, "end": v(-36.82, 5.24) * mm});
            skLineSegment(sketch, "E225", {"start": v(-37.2, 22.33) * mm, "end": v(14.76, 52.33) * mm});
            skLineSegment(sketch, "E226", {"start": v(28.42, 48.67) * mm, "end": v(43.42, 22.7) * mm});
            skPoint(sketch, "E227.visualSharp", {"position": v(23.42, 57.33) * mm});
            skArc(sketch, "E227.filletArc", {"start": v(28.42, 48.67) * mm, "mid": v(22.35, 53.33) * mm, "end": v(14.76, 52.33) * mm});
            skPoint(sketch, "E228.visualSharp", {"position": v(48.42, 14.03) * mm});
            skArc(sketch, "E228.filletArc", {"start": v(39.76, 9.03) * mm, "mid": v(44.42, 15.1) * mm, "end": v(43.42, 22.7) * mm});
            skLineSegment(sketch, "E229", {"start": v(35.92, 35.68) * mm, "end": v(9.94, 20.68) * mm, "construction": true});
            skLineSegment(sketch, "E230", {"start": v(-11.22, 37.33) * mm, "end": v(-9.72, 34.73) * mm, "construction": true});
            skLineSegment(sketch, "E231", {"start": v(-5.04, 37.44) * mm, "end": v(-35.7, 19.73) * mm});
            skLineSegment(sketch, "E232.0", {"start": v(-3.54, 34.84) * mm, "end": v(-34.2, 17.14) * mm});
            skArc(sketch, "E233", {"start": v(-3.54, 34.84) * mm, "mid": v(-3, 36.89) * mm, "end": v(-5.04, 37.44) * mm});
            skArc(sketch, "E234", {"start": v(-35.7, 19.73) * mm, "mid": v(-36.25, 17.69) * mm, "end": v(-34.2, 17.14) * mm});
            skLineSegment(sketch, "E235", {"start": v(-5.04, 37.44) * mm, "end": v(16.26, 49.73) * mm, "construction": true});
            skLineSegment(sketch, "E236", {"start": v(-3.54, 34.84) * mm, "end": v(17.76, 47.14) * mm, "construction": true});
            skLineSegment(sketch, "E237", {"start": v(16.26, 49.73) * mm, "end": v(17.76, 47.14) * mm, "construction": true});
            skCircle(sketch, "E238", {"center": v(17, 48.44) * mm, "radius": 1.5 * mm});
            skLineSegment(sketch, "E239.0", {"start": v(24.17, 0.03) * mm, "end": v(-0.83, 43.33) * mm, "construction": true});
            skLineSegment(sketch, "E240", {"start": v(7.44, 25.01) * mm, "end": v(2.44, 33.67) * mm});
            skLineSegment(sketch, "E241", {"start": v(12.44, 16.35) * mm, "end": v(17.44, 7.7) * mm});
            skLineSegment(sketch, "E242.0", {"start": v(22.44, -0.97) * mm, "end": v(-2.56, 42.33) * mm, "construction": true});
            skLineSegment(sketch, "E243", {"start": v(17.44, 7.7) * mm, "end": v(19.17, 8.7) * mm});
            skLineSegment(sketch, "E244", {"start": v(12.44, 16.35) * mm, "end": v(14.17, 17.35) * mm});
            skLineSegment(sketch, "E245", {"start": v(7.44, 25.01) * mm, "end": v(9.17, 26.01) * mm});
            skLineSegment(sketch, "E246", {"start": v(2.44, 33.67) * mm, "end": v(4.17, 34.67) * mm});
            skLineSegment(sketch, "E247", {"start": v(4.17, 34.67) * mm, "end": v(9.17, 26.01) * mm});
            skLineSegment(sketch, "E248", {"start": v(14.17, 17.35) * mm, "end": v(19.17, 8.7) * mm});
            skLineSegment(sketch, "E249", {"start": v(-10.04, 22.84) * mm, "end": v(-10.04, 21.84) * mm});
            skLineSegment(sketch, "E250", {"start": v(-10.04, 21.84) * mm, "end": v(-13.54, 21.84) * mm, "construction": true});
            skCircle(sketch, "E251", {"center": v(-13.54, 21.84) * mm, "radius": 3.5 * mm, "construction": true});
            skLineSegment(sketch, "E252.0", {"start": v(22.36, 45.17) * mm, "end": v(27.1, 36.95) * mm});
            skArc(sketch, "E253.0", {"start": v(36.26, 15.1) * mm, "mid": v(37.66, 16.92) * mm, "end": v(37.36, 19.2) * mm});
            skArc(sketch, "E254.0", {"start": v(22.36, 45.17) * mm, "mid": v(20.53, 46.57) * mm, "end": v(18.26, 46.27) * mm});
            skLineSegment(sketch, "E255", {"start": v(23.5, 11.2) * mm, "end": v(18.75, 19.42) * mm});
            skLineSegment(sketch, "E256.trimOffspring", {"start": v(9.6, 41.27) * mm, "end": v(15.02, 44.4) * mm});
            skPoint(sketch, "E257.visualSharp", {"position": v(7, 39.77) * mm});
            skArc(sketch, "E257.filletArc", {"start": v(9.6, 41.27) * mm, "mid": v(8.2, 39.45) * mm, "end": v(8.5, 37.17) * mm});
            skLineSegment(sketch, "E258", {"start": v(36.26, 15.1) * mm, "end": v(27.6, 10.1) * mm});
            skPoint(sketch, "E259.visualSharp", {"position": v(25, 8.6) * mm});
            skArc(sketch, "E259.filletArc", {"start": v(23.5, 11.2) * mm, "mid": v(25.32, 9.8) * mm, "end": v(27.6, 10.1) * mm});
            skLineSegment(sketch, "E260.0", {"start": v(26, 32.85) * mm, "end": v(17.35, 27.85) * mm});
            skLineSegment(sketch, "E261.0", {"start": v(28.5, 28.52) * mm, "end": v(19.85, 23.52) * mm});
            skLineSegment(sketch, "E262.trimOffspring", {"start": v(32.6, 27.42) * mm, "end": v(37.36, 19.2) * mm});
            skLineSegment(sketch, "E263.trimOffspring", {"start": v(13.25, 28.95) * mm, "end": v(8.5, 37.17) * mm});
            skPoint(sketch, "E264.visualSharp", {"position": v(31.1, 30.02) * mm});
            skArc(sketch, "E264.filletArc", {"start": v(32.6, 27.42) * mm, "mid": v(30.78, 28.82) * mm, "end": v(28.5, 28.52) * mm});
            skPoint(sketch, "E265.visualSharp", {"position": v(17.25, 22.02) * mm});
            skArc(sketch, "E265.filletArc", {"start": v(19.85, 23.52) * mm, "mid": v(18.45, 21.7) * mm, "end": v(18.75, 19.42) * mm});
            skPoint(sketch, "E266.visualSharp", {"position": v(14.75, 26.35) * mm});
            skArc(sketch, "E266.filletArc", {"start": v(13.25, 28.95) * mm, "mid": v(15.07, 27.55) * mm, "end": v(17.35, 27.85) * mm});
            skPoint(sketch, "E267.visualSharp", {"position": v(28.6, 34.35) * mm});
            skArc(sketch, "E267.filletArc", {"start": v(26, 32.85) * mm, "mid": v(27.4, 34.67) * mm, "end": v(27.1, 36.95) * mm});
            skLineSegment(sketch, "E268", {"start": v(9.18, -2.21) * mm, "end": v(-10.82, -2.21) * mm, "construction": true});
            skLineSegment(sketch, "E269", {"start": v(-10.82, -2.21) * mm, "end": v(-5.82, -2.21) * mm});
            skLineSegment(sketch, "E270", {"start": v(-5.82, -2.21) * mm, "end": v(-5.82, 33.52) * mm, "construction": true});
            skLineSegment(sketch, "E271", {"start": v(-5.82, -2.21) * mm, "end": v(-5.82, 12.79) * mm});
            skLineSegment(sketch, "E272", {"start": v(-5.82, 12.79) * mm, "end": v(-5.82, 14.79) * mm});
            skLineSegment(sketch, "E273.bottom", {"start": v(-10.82, 12.79) * mm, "end": v(-0.82, 12.79) * mm});
            skLineSegment(sketch, "E273.top", {"start": v(-10.82, 14.79) * mm, "end": v(-0.82, 14.79) * mm});
            skLineSegment(sketch, "E273.left", {"start": v(-10.82, 12.79) * mm, "end": v(-10.82, 14.79) * mm});
            skLineSegment(sketch, "E273.right", {"start": v(-0.82, 12.79) * mm, "end": v(-0.82, 14.79) * mm});
            skPoint(sketch, "E273.middle", {"position": v(-5.82, 13.79) * mm});
            skLineSegment(sketch, "E274.bottom", {"start": v(-22.32, 3.79) * mm, "end": v(10.68, 3.79) * mm});
            skLineSegment(sketch, "E274.top", {"start": v(-22.32, 6.79) * mm, "end": v(10.68, 6.79) * mm});
            skLineSegment(sketch, "E274.left", {"start": v(-23.32, 4.79) * mm, "end": v(-23.32, 5.79) * mm});
            skLineSegment(sketch, "E274.right", {"start": v(11.68, 4.79) * mm, "end": v(11.68, 5.79) * mm});
            skPoint(sketch, "E274.middle", {"position": v(-5.82, 5.29) * mm});
            skPoint(sketch, "E275.visualSharp", {"position": v(11.68, 6.79) * mm});
            skArc(sketch, "E275.filletArc", {"start": v(11.68, 5.79) * mm, "mid": v(11.39, 6.5) * mm, "end": v(10.68, 6.79) * mm});
            skPoint(sketch, "E276.visualSharp", {"position": v(11.68, 3.79) * mm});
            skArc(sketch, "E276.filletArc", {"start": v(10.68, 3.79) * mm, "mid": v(11.39, 4.08) * mm, "end": v(11.68, 4.79) * mm});
            skPoint(sketch, "E277.visualSharp", {"position": v(-23.32, 3.79) * mm});
            skArc(sketch, "E277.filletArc", {"start": v(-23.32, 4.79) * mm, "mid": v(-23.03, 4.08) * mm, "end": v(-22.32, 3.79) * mm});
            skPoint(sketch, "E278.visualSharp", {"position": v(-23.32, 6.79) * mm});
            skArc(sketch, "E278.filletArc", {"start": v(-22.32, 6.79) * mm, "mid": v(-23.03, 6.5) * mm, "end": v(-23.32, 5.79) * mm});
            skLineSegment(sketch, "E279", {"start": v(17.76, 47.14) * mm, "end": v(19.26, 44.54) * mm, "construction": true});
            skArc(sketch, "E280", {"start": v(15.02, 44.4) * mm, "mid": v(17.16, 43.94) * mm, "end": v(19.26, 44.54) * mm});
            skLineSegment(sketch, "E281", {"start": v(19.26, 44.54) * mm, "end": v(21.7, 45.95) * mm});
            skLineSegment(sketch, "E282", {"start": v(15.02, 44.4) * mm, "end": v(18.26, 46.27) * mm, "construction": true});
            skLineSegment(sketch, "E283", {"start": v(-13.54, 21.84) * mm, "end": v(-13.54, 19.84) * mm, "construction": true});
            skCircle(sketch, "E284", {"center": v(-13.54, 19.84) * mm, "radius": 3.5 * mm});
            skSolve(sketch);
        }
        {
            var Q0;
            Q0 = qSketchRegion(id + "F19", true);
            extrude(context, id + "F20", {"entities" : qUnion([Q0]), "depth" : 2 * mm});
        }
        {
            var Q0;
            Q0 = qSketchRegion(id + "F2", true);
            extrude(context, id + "F21", {"entities" : qUnion([Q0]), "depth" : 40 * mm});
        }
        {
            var Q0;
            Q0 = qSketchRegion(id + "F2", true);
            extrude(context, id + "F22", {"entities" : qUnion([Q0]), "depth" : 15 * mm});
        }
        {
            var Q0;
            Q0=qCreatedBy(makeId("Top.planeOp"),FACE);
            var sketch = newSketch(context, id + "F23", { "sketchPlane" : qUnion([Q0])});
            skLineSegment(sketch, "E285.bottom", {"start": v(17.96, -16.25) * mm, "end": v(-22.04, -16.25) * mm});
            skLineSegment(sketch, "E285.top", {"start": v(17.96, 18.75) * mm, "end": v(-22.04, 18.75) * mm});
            skPoint(sketch, "E285.middle", {"position": v(-2.04, 1.25) * mm});
            skLineSegment(sketch, "E286", {"start": v(-22.04, -16.25) * mm, "end": v(-22.04, 8.75) * mm});
            skLineSegment(sketch, "E287", {"start": v(17.96, 8.75) * mm, "end": v(17.96, -16.25) * mm});
            skCircle(sketch, "E288", {"center": v(-18.54, 13.76) * mm, "radius": 1.5 * mm});
            skLineSegment(sketch, "E289", {"start": v(17.96, 13.76) * mm, "end": v(14.46, 13.76) * mm, "construction": true});
            skCircle(sketch, "E290", {"center": v(14.46, 13.76) * mm, "radius": 1.5 * mm});
            skLineSegment(sketch, "E291", {"start": v(-22.04, 18.75) * mm, "end": v(-24.04, 18.75) * mm});
            skLineSegment(sketch, "E292", {"start": v(-24.04, 18.75) * mm, "end": v(-24.04, 8.75) * mm});
            skLineSegment(sketch, "E293", {"start": v(-24.04, 8.75) * mm, "end": v(-22.04, 8.75) * mm});
            skLineSegment(sketch, "E294.MirrorCS", {"start": v(19.96, 18.75) * mm, "end": v(19.96, 8.75) * mm});
            skLineSegment(sketch, "E295.MirrorCS", {"start": v(19.96, 8.75) * mm, "end": v(17.96, 8.75) * mm});
            skLineSegment(sketch, "E296.MirrorCS", {"start": v(17.96, 18.75) * mm, "end": v(19.96, 18.75) * mm});
            skLineSegment(sketch, "E297", {"start": v(17.96, 8.75) * mm, "end": v(17.96, 18.75) * mm, "construction": true});
            skLineSegment(sketch, "E298", {"start": v(-22.04, 18.75) * mm, "end": v(-22.04, 8.75) * mm, "construction": true});
            skLineSegment(sketch, "E299", {"start": v(-2.04, -16.25) * mm, "end": v(-2.04, -11.25) * mm});
            skLineSegment(sketch, "E300", {"start": v(-2.04, -11.25) * mm, "end": v(-2.04, -8.25) * mm});
            skLineSegment(sketch, "E301", {"start": v(-2.04, -8.25) * mm, "end": v(-2.04, -3.25) * mm});
            skLineSegment(sketch, "E302", {"start": v(-2.04, -3.25) * mm, "end": v(-2.04, -0.25) * mm});
            skLineSegment(sketch, "E303.bottom", {"start": v(11.96, -11.25) * mm, "end": v(-16.04, -11.25) * mm});
            skLineSegment(sketch, "E303.top", {"start": v(11.96, -8.25) * mm, "end": v(-16.04, -8.25) * mm});
            skLineSegment(sketch, "E303.left", {"start": v(12.96, -10.25) * mm, "end": v(12.96, -9.25) * mm});
            skLineSegment(sketch, "E303.right", {"start": v(-17.04, -10.25) * mm, "end": v(-17.04, -9.25) * mm});
            skPoint(sketch, "E303.middle", {"position": v(-2.04, -9.75) * mm});
            skLineSegment(sketch, "E304.bottom", {"start": v(11.96, -3.25) * mm, "end": v(-16.04, -3.25) * mm});
            skLineSegment(sketch, "E304.top", {"start": v(11.96, -0.25) * mm, "end": v(-16.04, -0.25) * mm});
            skLineSegment(sketch, "E304.left", {"start": v(12.96, -2.25) * mm, "end": v(12.96, -1.25) * mm});
            skLineSegment(sketch, "E304.right", {"start": v(-17.04, -2.25) * mm, "end": v(-17.04, -1.25) * mm});
            skPoint(sketch, "E304.middle", {"position": v(-2.04, -1.75) * mm});
            skLineSegment(sketch, "E305", {"start": v(-2.04, -0.25) * mm, "end": v(-2.04, 4.75) * mm});
            skLineSegment(sketch, "E306", {"start": v(-2.04, 4.75) * mm, "end": v(-2.04, 7.75) * mm});
            skLineSegment(sketch, "E307.bottom", {"start": v(11.96, 4.75) * mm, "end": v(-16.04, 4.75) * mm});
            skLineSegment(sketch, "E307.top", {"start": v(11.96, 7.75) * mm, "end": v(-16.04, 7.75) * mm});
            skLineSegment(sketch, "E307.left", {"start": v(12.96, 5.75) * mm, "end": v(12.96, 6.75) * mm});
            skLineSegment(sketch, "E307.right", {"start": v(-17.04, 5.75) * mm, "end": v(-17.04, 6.75) * mm});
            skPoint(sketch, "E307.middle", {"position": v(-2.04, 6.25) * mm});
            skPoint(sketch, "E308.visualSharp", {"position": v(-17.04, 7.75) * mm});
            skArc(sketch, "E308.filletArc", {"start": v(-16.04, 7.75) * mm, "mid": v(-16.75, 7.46) * mm, "end": v(-17.04, 6.75) * mm});
            skPoint(sketch, "E309.visualSharp", {"position": v(-17.04, 4.75) * mm});
            skArc(sketch, "E309.filletArc", {"start": v(-17.04, 5.75) * mm, "mid": v(-16.75, 5.05) * mm, "end": v(-16.04, 4.75) * mm});
            skPoint(sketch, "E310.visualSharp", {"position": v(12.96, 4.75) * mm});
            skArc(sketch, "E310.filletArc", {"start": v(11.96, 4.75) * mm, "mid": v(12.67, 5.05) * mm, "end": v(12.96, 5.75) * mm});
            skPoint(sketch, "E311.visualSharp", {"position": v(12.96, 7.75) * mm});
            skArc(sketch, "E311.filletArc", {"start": v(12.96, 6.75) * mm, "mid": v(12.67, 7.46) * mm, "end": v(11.96, 7.75) * mm});
            skPoint(sketch, "E312.visualSharp", {"position": v(12.96, -0.25) * mm});
            skArc(sketch, "E312.filletArc", {"start": v(12.96, -1.25) * mm, "mid": v(12.67, -0.54) * mm, "end": v(11.96, -0.25) * mm});
            skPoint(sketch, "E313.visualSharp", {"position": v(12.96, -3.25) * mm});
            skArc(sketch, "E313.filletArc", {"start": v(11.96, -3.25) * mm, "mid": v(12.67, -2.95) * mm, "end": v(12.96, -2.25) * mm});
            skPoint(sketch, "E314.visualSharp", {"position": v(-17.04, -3.25) * mm});
            skArc(sketch, "E314.filletArc", {"start": v(-17.04, -2.25) * mm, "mid": v(-16.75, -2.95) * mm, "end": v(-16.04, -3.25) * mm});
            skPoint(sketch, "E315.visualSharp", {"position": v(-17.04, -0.25) * mm});
            skArc(sketch, "E315.filletArc", {"start": v(-16.04, -0.25) * mm, "mid": v(-16.75, -0.54) * mm, "end": v(-17.04, -1.25) * mm});
            skPoint(sketch, "E316.visualSharp", {"position": v(-17.04, -8.25) * mm});
            skArc(sketch, "E316.filletArc", {"start": v(-16.04, -8.25) * mm, "mid": v(-16.75, -8.54) * mm, "end": v(-17.04, -9.25) * mm});
            skPoint(sketch, "E317.visualSharp", {"position": v(12.96, -8.25) * mm});
            skArc(sketch, "E317.filletArc", {"start": v(12.96, -9.25) * mm, "mid": v(12.67, -8.54) * mm, "end": v(11.96, -8.25) * mm});
            skPoint(sketch, "E318.visualSharp", {"position": v(12.96, -11.25) * mm});
            skArc(sketch, "E318.filletArc", {"start": v(11.96, -11.25) * mm, "mid": v(12.67, -10.95) * mm, "end": v(12.96, -10.25) * mm});
            skPoint(sketch, "E319.visualSharp", {"position": v(-17.04, -11.25) * mm});
            skArc(sketch, "E319.filletArc", {"start": v(-17.04, -10.25) * mm, "mid": v(-16.75, -10.95) * mm, "end": v(-16.04, -11.25) * mm});
            skSolve(sketch);
        }
        {
            var Q0;
            Q0 = qSketchRegion(id + "F23", true);
            extrude(context, id + "F24", {"entities" : qUnion([Q0]), "depth" : 2 * mm});
        }
        {
            var Q0;
            Q0=qCreatedBy(makeId("Top.planeOp"),FACE);
            var sketch = newSketch(context, id + "F25", { "sketchPlane" : qUnion([Q0])});
            skLineSegment(sketch, "E320.bottom", {"start": v(17.46, -9.47) * mm, "end": v(-22.54, -9.47) * mm});
            skLineSegment(sketch, "E320.top", {"start": v(17.46, 30.53) * mm, "end": v(-22.54, 30.53) * mm});
            skPoint(sketch, "E320.middle", {"position": v(-2.54, 10.53) * mm});
            skLineSegment(sketch, "E321", {"start": v(17.46, 25.53) * mm, "end": v(19.46, 25.53) * mm});
            skLineSegment(sketch, "E322", {"start": v(19.46, 25.53) * mm, "end": v(19.46, 15.53) * mm});
            skLineSegment(sketch, "E323", {"start": v(19.46, 15.53) * mm, "end": v(17.46, 15.53) * mm});
            skLineSegment(sketch, "E324.MirrorCS", {"start": v(17.46, -4.47) * mm, "end": v(19.46, -4.47) * mm});
            skLineSegment(sketch, "E325.MirrorCS", {"start": v(19.46, -4.47) * mm, "end": v(19.46, 5.53) * mm});
            skLineSegment(sketch, "E326.MirrorCS", {"start": v(19.46, 5.53) * mm, "end": v(17.46, 5.53) * mm});
            skLineSegment(sketch, "E327.MirrorCS", {"start": v(-22.54, 25.53) * mm, "end": v(-24.54, 25.53) * mm});
            skLineSegment(sketch, "E328.MirrorCS", {"start": v(-24.54, 5.53) * mm, "end": v(-22.54, 5.53) * mm});
            skLineSegment(sketch, "E329.MirrorCS", {"start": v(-24.54, 15.53) * mm, "end": v(-22.54, 15.53) * mm});
            skLineSegment(sketch, "E330.MirrorCS", {"start": v(-22.54, -4.47) * mm, "end": v(-24.54, -4.47) * mm});
            skLineSegment(sketch, "E331.MirrorCS", {"start": v(-24.54, -4.47) * mm, "end": v(-24.54, 5.53) * mm});
            skLineSegment(sketch, "E332.MirrorCS", {"start": v(-24.54, 25.53) * mm, "end": v(-24.54, 15.53) * mm});
            skLineSegment(sketch, "E333", {"start": v(-22.54, 30.53) * mm, "end": v(-22.54, 25.53) * mm});
            skLineSegment(sketch, "E334", {"start": v(-22.54, 25.53) * mm, "end": v(-22.54, 15.53) * mm, "construction": true});
            skLineSegment(sketch, "E335", {"start": v(-22.54, 15.53) * mm, "end": v(-22.54, 5.53) * mm});
            skLineSegment(sketch, "E336", {"start": v(-22.54, 5.53) * mm, "end": v(-22.54, -4.47) * mm, "construction": true});
            skLineSegment(sketch, "E337", {"start": v(-22.54, -4.47) * mm, "end": v(-22.54, -9.47) * mm});
            skLineSegment(sketch, "E338", {"start": v(17.46, 30.53) * mm, "end": v(17.46, 25.53) * mm});
            skLineSegment(sketch, "E339", {"start": v(17.46, 15.53) * mm, "end": v(17.46, 5.53) * mm});
            skLineSegment(sketch, "E340", {"start": v(17.46, -4.47) * mm, "end": v(17.46, -9.47) * mm});
            skLineSegment(sketch, "E341", {"start": v(17.46, 25.53) * mm, "end": v(17.46, 15.53) * mm, "construction": true});
            skLineSegment(sketch, "E342", {"start": v(17.46, 5.53) * mm, "end": v(17.46, -4.47) * mm, "construction": true});
            skLineSegment(sketch, "E343.bottom", {"start": v(11.46, -3.47) * mm, "end": v(-16.54, -3.47) * mm, "construction": true});
            skLineSegment(sketch, "E343.top", {"start": v(11.46, 24.53) * mm, "end": v(-16.54, 24.53) * mm, "construction": true});
            skLineSegment(sketch, "E343.left", {"start": v(11.46, -3.47) * mm, "end": v(11.46, 24.53) * mm, "construction": true});
            skLineSegment(sketch, "E343.right", {"start": v(-16.54, -3.47) * mm, "end": v(-16.54, 24.53) * mm, "construction": true});
            skCircle(sketch, "E344", {"center": v(11.46, 24.53) * mm, "radius": 1 * mm});
            skCircle(sketch, "E345", {"center": v(-16.54, 24.53) * mm, "radius": 1 * mm});
            skCircle(sketch, "E346", {"center": v(11.46, -3.47) * mm, "radius": 1 * mm});
            skCircle(sketch, "E347", {"center": v(-16.54, -3.47) * mm, "radius": 1 * mm});
            skCircle(sketch, "E348", {"center": v(-2.54, 10.53) * mm, "radius": 12.5 * mm});
            skSolve(sketch);
        }
        {
            var Q0;
            Q0 = qSketchRegion(id + "F25", true);
            extrude(context, id + "F26", {"entities" : qUnion([Q0]), "depth" : 2 * mm});
        }
        {
            var Q0;
            Q0=qCreatedBy(makeId("Top.planeOp"),FACE);
            var sketch = newSketch(context, id + "F27", { "sketchPlane" : qUnion([Q0])});
            skLineSegment(sketch, "E349.bottom", {"start": v(-0.02, -7.12) * mm, "end": v(-49.02, -7.12) * mm});
            skLineSegment(sketch, "E349.top", {"start": v(-0.02, 7.88) * mm, "end": v(-49.02, 7.88) * mm});
            skLineSegment(sketch, "E349.left", {"start": v(-0.02, -7.12) * mm, "end": v(-0.02, 7.88) * mm});
            skLineSegment(sketch, "E349.right", {"start": v(-49.02, -7.12) * mm, "end": v(-49.02, 7.88) * mm});
            skPoint(sketch, "E349.middle", {"position": v(-24.52, 0.38) * mm});
            skSolve(sketch);
        }
        {
            var Q0;
            Q0 = qSketchRegion(id + "F27", true);
            extrude(context, id + "F28", {"entities" : qUnion([Q0]), "depth" : 2 * mm});
        }
        {
            var Q0;
            Q0=qCreatedBy(makeId("Top.planeOp"),FACE);
            var sketch = newSketch(context, id + "F29", { "sketchPlane" : qUnion([Q0])});
            skLineSegment(sketch, "E350.bottom", {"start": v(-11.72, 21.48) * mm, "end": v(8.28, 21.48) * mm});
            skLineSegment(sketch, "E350.top", {"start": v(-11.72, -12.02) * mm, "end": v(8.28, -12.02) * mm});
            skLineSegment(sketch, "E350.left", {"start": v(-11.72, 21.48) * mm, "end": v(-11.72, -12.02) * mm});
            skLineSegment(sketch, "E350.right", {"start": v(8.28, 21.48) * mm, "end": v(8.28, -12.02) * mm});
            skLineSegment(sketch, "E351.bottom", {"start": v(-11.72, 21.48) * mm, "end": v(-9.72, 21.48) * mm});
            skLineSegment(sketch, "E351.top", {"start": v(-11.72, 21.48) * mm, "end": v(-9.72, 21.48) * mm});
            skLineSegment(sketch, "E351.left", {"start": v(-11.72, 21.48) * mm, "end": v(-11.72, 21.48) * mm});
            skLineSegment(sketch, "E351.right", {"start": v(-9.72, 21.48) * mm, "end": v(-9.72, 21.48) * mm});
            skLineSegment(sketch, "E352", {"start": v(-9.72, 21.48) * mm, "end": v(-9.72, 31.48) * mm});
            skLineSegment(sketch, "E353", {"start": v(-9.72, 31.48) * mm, "end": v(-2.72, 31.48) * mm});
            skLineSegment(sketch, "E354", {"start": v(-2.72, 31.48) * mm, "end": v(-2.72, 21.48) * mm});
            skSolve(sketch);
        }
        {
            var Q0;
            Q0 = qSketchRegion(id + "F29", true);
            extrude(context, id + "F30", {"entities" : qUnion([Q0]), "depth" : 7 * mm});
        }
        {
            var Q0;
            Q0=qCreatedBy(makeId("Top.planeOp"),FACE);
            var sketch = newSketch(context, id + "F31", { "sketchPlane" : qUnion([Q0])});
            skLineSegment(sketch, "E355.bottom", {"start": v(-25.4, -22.9) * mm, "end": v(-15.38, -22.9) * mm});
            skLineSegment(sketch, "E356.top", {"start": v(4.62, -24.9) * mm, "end": v(-15.38, -24.9) * mm});
            skLineSegment(sketch, "E356.left", {"start": v(4.62, -22.9) * mm, "end": v(4.62, -24.9) * mm});
            skLineSegment(sketch, "E356.right", {"start": v(-15.38, -22.9) * mm, "end": v(-15.38, -24.9) * mm});
            skLineSegment(sketch, "E357.trimOffspring", {"start": v(4.62, -22.9) * mm, "end": v(15.72, -22.9) * mm});
            skLineSegment(sketch, "E358", {"start": v(15.72, -22.9) * mm, "end": v(35.2, -11.66) * mm});
            skLineSegment(sketch, "E359", {"start": v(-25.4, -22.9) * mm, "end": v(-41.38, -15.46) * mm});
            skLineSegment(sketch, "E360", {"start": v(-44.27, -2.7) * mm, "end": v(-44.27, -10.92) * mm});
            skPoint(sketch, "E361.visualSharp", {"position": v(-44.27, -14.1) * mm});
            skArc(sketch, "E361.filletArc", {"start": v(-44.27, -10.92) * mm, "mid": v(-43.48, -13.61) * mm, "end": v(-41.38, -15.46) * mm});
            skLineSegment(sketch, "E362", {"start": v(23.86, 27.98) * mm, "end": v(38.86, 2) * mm});
            skPoint(sketch, "E363.visualSharp", {"position": v(18.86, 36.64) * mm});
            skPoint(sketch, "E364.visualSharp", {"position": v(43.86, -6.66) * mm});
            skArc(sketch, "E364.filletArc", {"start": v(35.2, -11.66) * mm, "mid": v(39.86, -5.6) * mm, "end": v(38.86, 2) * mm});
            skLineSegment(sketch, "E365", {"start": v(-15.78, 16.64) * mm, "end": v(-14.28, 14.04) * mm, "construction": true});
            skLineSegment(sketch, "E366", {"start": v(-9.6, 16.74) * mm, "end": v(-40.27, -0.96) * mm});
            skLineSegment(sketch, "E367.0", {"start": v(-8.1, 14.14) * mm, "end": v(-38.77, -3.56) * mm});
            skArc(sketch, "E368", {"start": v(-8.1, 14.14) * mm, "mid": v(-7.55, 16.2) * mm, "end": v(-9.6, 16.74) * mm});
            skArc(sketch, "E369", {"start": v(-40.27, -0.96) * mm, "mid": v(-40.81, -3) * mm, "end": v(-38.77, -3.56) * mm});
            skLineSegment(sketch, "E370", {"start": v(2.88, 4.32) * mm, "end": v(-2.12, 12.98) * mm});
            skLineSegment(sketch, "E371", {"start": v(7.88, -4.34) * mm, "end": v(12.88, -13) * mm});
            skLineSegment(sketch, "E372", {"start": v(12.88, -13) * mm, "end": v(14.6, -12) * mm});
            skLineSegment(sketch, "E373", {"start": v(7.88, -4.34) * mm, "end": v(9.6, -3.34) * mm});
            skLineSegment(sketch, "E374", {"start": v(2.88, 4.32) * mm, "end": v(4.6, 5.32) * mm});
            skLineSegment(sketch, "E375", {"start": v(-2.12, 12.98) * mm, "end": v(-0.4, 13.98) * mm});
            skLineSegment(sketch, "E376", {"start": v(-0.4, 13.98) * mm, "end": v(4.6, 5.32) * mm});
            skLineSegment(sketch, "E377", {"start": v(9.6, -3.34) * mm, "end": v(14.6, -12) * mm});
            skLineSegment(sketch, "E378", {"start": v(4.62, -22.9) * mm, "end": v(-15.38, -22.9) * mm, "construction": true});
            skLineSegment(sketch, "E379", {"start": v(-15.38, -22.9) * mm, "end": v(-10.38, -22.9) * mm});
            skLineSegment(sketch, "E380.0", {"start": v(-15.38, -14.9) * mm, "end": v(-5.38, -14.9) * mm});
            skLineSegment(sketch, "E381.0", {"start": v(-15.38, -12.9) * mm, "end": v(-5.38, -12.9) * mm});
            skLineSegment(sketch, "E382", {"start": v(-5.38, -12.9) * mm, "end": v(-5.38, -14.9) * mm});
            skLineSegment(sketch, "E383", {"start": v(-15.38, -12.9) * mm, "end": v(-15.38, -14.9) * mm});
            skLineSegment(sketch, "E384", {"start": v(-8.85, 15.44) * mm, "end": v(-8.85, 8.44) * mm, "construction": true});
            skLineSegment(sketch, "E385", {"start": v(-9.6, 9.74) * mm, "end": v(-40.27, -7.96) * mm});
            skLineSegment(sketch, "E386.0", {"start": v(-8.1, 7.14) * mm, "end": v(-38.77, -10.56) * mm});
            skArc(sketch, "E387", {"start": v(-8.1, 7.14) * mm, "mid": v(-7.55, 9.2) * mm, "end": v(-9.6, 9.74) * mm});
            skArc(sketch, "E388", {"start": v(-40.27, -7.96) * mm, "mid": v(-40.81, -10) * mm, "end": v(-38.77, -10.56) * mm});
            skCircle(sketch, "E389", {"center": v(15.48, 22.5) * mm, "radius": 1.5 * mm});
            skLineSegment(sketch, "E390.0", {"start": v(21.82, 17.5) * mm, "end": v(32.8, -1.5) * mm});
            skArc(sketch, "E391.0", {"start": v(31.7, -5.6) * mm, "mid": v(33.1, -3.78) * mm, "end": v(32.8, -1.5) * mm});
            skLineSegment(sketch, "E392.0", {"start": v(23.9, -10.1) * mm, "end": v(31.7, -5.6) * mm});
            skLineSegment(sketch, "E393.0", {"start": v(7.33, 12.6) * mm, "end": v(19.8, -9) * mm});
            skPoint(sketch, "E394.visualSharp", {"position": v(21.3, -11.6) * mm});
            skArc(sketch, "E394.filletArc", {"start": v(19.8, -9) * mm, "mid": v(21.63, -10.4) * mm, "end": v(23.9, -10.1) * mm});
            skLineSegment(sketch, "E395", {"start": v(17.73, 18.6) * mm, "end": v(16.43, 17.84) * mm});
            skLineSegment(sketch, "E396", {"start": v(11.58, 20.24) * mm, "end": v(12.33, 18.94) * mm});
            skLineSegment(sketch, "E397", {"start": v(11.58, 20.24) * mm, "end": v(11.3, 20.73) * mm});
            skLineSegment(sketch, "E398", {"start": v(7.33, 12.6) * mm, "end": v(4.8, 16.98) * mm});
            skPoint(sketch, "E399.visualSharp", {"position": v(20.32, 20.1) * mm});
            skArc(sketch, "E399.filletArc", {"start": v(21.82, 17.5) * mm, "mid": v(20, 18.9) * mm, "end": v(17.73, 18.6) * mm});
            skPoint(sketch, "E400.visualSharp", {"position": v(13.83, 16.34) * mm});
            skArc(sketch, "E400.filletArc", {"start": v(12.33, 18.94) * mm, "mid": v(14.15, 17.54) * mm, "end": v(16.43, 17.84) * mm});
            skLineSegment(sketch, "E401", {"start": v(-8.85, 15.44) * mm, "end": v(-8.85, 22.44) * mm, "construction": true});
            skLineSegment(sketch, "E402", {"start": v(-9.6, 23.74) * mm, "end": v(-40.27, 6.04) * mm});
            skLineSegment(sketch, "E403.0", {"start": v(-8.1, 21.14) * mm, "end": v(-38.77, 3.44) * mm});
            skArc(sketch, "E404", {"start": v(-8.1, 21.14) * mm, "mid": v(-7.55, 23.2) * mm, "end": v(-9.6, 23.74) * mm});
            skArc(sketch, "E405", {"start": v(-40.27, 6.04) * mm, "mid": v(-40.81, 4) * mm, "end": v(-38.77, 3.44) * mm});
            skLineSegment(sketch, "E406.0", {"start": v(-11.1, 26.34) * mm, "end": v(-41.77, 8.64) * mm});
            skLineSegment(sketch, "E407", {"start": v(-44.27, -2.7) * mm, "end": v(-44.27, 4.3) * mm});
            skLineSegment(sketch, "E408", {"start": v(23.86, 27.98) * mm, "end": v(20.82, 33.23) * mm});
            skLineSegment(sketch, "E409", {"start": v(-11.1, 26.34) * mm, "end": v(7.16, 36.89) * mm});
            skArc(sketch, "E410.filletArc", {"start": v(20.82, 33.23) * mm, "mid": v(14.75, 37.89) * mm, "end": v(7.16, 36.89) * mm});
            skPoint(sketch, "E411.visualSharp", {"position": v(-44.27, 7.2) * mm});
            skArc(sketch, "E411.filletArc", {"start": v(-41.77, 8.64) * mm, "mid": v(-43.6, 6.8) * mm, "end": v(-44.27, 4.3) * mm});
            skLineSegment(sketch, "E412", {"start": v(11.58, 20.24) * mm, "end": v(10.83, 21.54) * mm});
            skLineSegment(sketch, "E413", {"start": v(13.23, 26.39) * mm, "end": v(11.93, 25.64) * mm});
            skPoint(sketch, "E414.visualSharp", {"position": v(9.33, 24.14) * mm});
            skArc(sketch, "E414.filletArc", {"start": v(11.93, 25.64) * mm, "mid": v(10.53, 23.82) * mm, "end": v(10.83, 21.54) * mm});
            skLineSegment(sketch, "E415", {"start": v(13.23, 26.39) * mm, "end": v(13.23, 26.39) * mm});
            skPoint(sketch, "E416.visualSharp", {"position": v(15.82, 27.89) * mm});
            skPoint(sketch, "E417.visualSharp", {"position": v(11.26, 35.79) * mm});
            skLineSegment(sketch, "E418", {"start": v(4.8, 16.98) * mm, "end": v(1.77, 22.23) * mm});
            skLineSegment(sketch, "E419.0", {"start": v(2.87, 26.33) * mm, "end": v(10.66, 30.83) * mm});
            skLineSegment(sketch, "E420", {"start": v(10.66, 30.83) * mm, "end": v(11.53, 31.33) * mm});
            skLineSegment(sketch, "E421", {"start": v(13.23, 26.39) * mm, "end": v(14.1, 26.89) * mm});
            skLineSegment(sketch, "E422.0", {"start": v(14.82, 29.62) * mm, "end": v(14.26, 30.6) * mm});
            skArc(sketch, "E423.filletArc", {"start": v(14.1, 26.89) * mm, "mid": v(15.02, 28.1) * mm, "end": v(14.82, 29.62) * mm});
            skPoint(sketch, "E424.visualSharp", {"position": v(13.26, 32.33) * mm});
            skArc(sketch, "E424.filletArc", {"start": v(14.26, 30.6) * mm, "mid": v(13.05, 31.53) * mm, "end": v(11.53, 31.33) * mm});
            skPoint(sketch, "E425.visualSharp", {"position": v(0.27, 24.83) * mm});
            skArc(sketch, "E425.filletArc", {"start": v(2.87, 26.33) * mm, "mid": v(1.47, 24.5) * mm, "end": v(1.77, 22.23) * mm});
            skCircle(sketch, "E426", {"center": v(-18.1, -8.87) * mm, "radius": 3 * mm});
            skLineSegment(sketch, "E427", {"start": v(2.88, 4.32) * mm, "end": v(7.88, -4.34) * mm, "construction": true});
            skLineSegment(sketch, "E428", {"start": v(-10.5, -0.02) * mm, "end": v(-5.52, 2.86) * mm});
            skLineSegment(sketch, "E429", {"start": v(2.45, -4.94) * mm, "end": v(-1.42, 1.76) * mm});
            skLineSegment(sketch, "E430.0", {"start": v(-9.73, -7.36) * mm, "end": v(-11.6, -4.12) * mm});
            skPoint(sketch, "E431.visualSharp", {"position": v(-2.92, 4.36) * mm});
            skArc(sketch, "E431.filletArc", {"start": v(-1.42, 1.76) * mm, "mid": v(-3.25, 3.16) * mm, "end": v(-5.52, 2.86) * mm});
            skPoint(sketch, "E432.visualSharp", {"position": v(-13.1, -1.52) * mm});
            skArc(sketch, "E432.filletArc", {"start": v(-10.5, -0.02) * mm, "mid": v(-11.9, -1.84) * mm, "end": v(-11.6, -4.12) * mm});
            skPoint(sketch, "E433.visualSharp", {"position": v(-8.53, -9.44) * mm});
            skLineSegment(sketch, "E434.0", {"start": v(-22.9, -16.55) * mm, "end": v(-26.46, -10.38) * mm});
            skLineSegment(sketch, "E435.0", {"start": v(-24.2, -17.95) * mm, "end": v(-32.07, -14.28) * mm});
            skLineSegment(sketch, "E436", {"start": v(-27.83, -10.02) * mm, "end": v(-32.14, -12.5) * mm});
            skPoint(sketch, "E437.visualSharp", {"position": v(-26.96, -9.52) * mm});
            skArc(sketch, "E437.filletArc", {"start": v(-26.46, -10.38) * mm, "mid": v(-27.07, -9.92) * mm, "end": v(-27.83, -10.02) * mm});
            skPoint(sketch, "E438.visualSharp", {"position": v(-33.8, -13.47) * mm});
            skArc(sketch, "E438.filletArc", {"start": v(-32.14, -12.5) * mm, "mid": v(-32.64, -13.42) * mm, "end": v(-32.07, -14.28) * mm});
            skPoint(sketch, "E439.visualSharp", {"position": v(-21.32, -19.3) * mm});
            skArc(sketch, "E439.filletArc", {"start": v(-24.2, -17.95) * mm, "mid": v(-23.03, -17.72) * mm, "end": v(-22.9, -16.55) * mm});
            skLineSegment(sketch, "E440", {"start": v(-18.1, -19.9) * mm, "end": v(-18.1, -16.9) * mm, "construction": true});
            skArc(sketch, "E441", {"start": v(-18.1, -16.9) * mm, "mid": v(-19.6, -18.4) * mm, "end": v(-18.1, -19.9) * mm});
            skLineSegment(sketch, "E442", {"start": v(12.72, -16.9) * mm, "end": v(12.72, -19.9) * mm, "construction": true});
            skLineSegment(sketch, "E443", {"start": v(-18.1, -16.9) * mm, "end": v(12.72, -16.9) * mm});
            skLineSegment(sketch, "E444", {"start": v(-18.1, -19.9) * mm, "end": v(12.72, -19.9) * mm});
            skArc(sketch, "E445", {"start": v(12.72, -19.9) * mm, "mid": v(14.22, -18.4) * mm, "end": v(12.72, -16.9) * mm});
            skLineSegment(sketch, "E446.0", {"start": v(-0.38, -13.48) * mm, "end": v(-0.38, -13.9) * mm, "construction": true});
            skPoint(sketch, "E447.visualSharp", {"position": v(-0.38, -14.9) * mm});
            skPoint(sketch, "E448.visualSharp", {"position": v(8.2, -14.9) * mm});
            skLineSegment(sketch, "E449", {"start": v(-3.03, -12.37) * mm, "end": v(-8.85, -8.32) * mm});
            skPoint(sketch, "E450.visualSharp", {"position": v(-9.4, -7.94) * mm});
            skArc(sketch, "E450.filletArc", {"start": v(-9.73, -7.36) * mm, "mid": v(-9.34, -7.9) * mm, "end": v(-8.85, -8.32) * mm});
            skPoint(sketch, "E451.visualSharp", {"position": v(0.62, -14.9) * mm});
            skLineSegment(sketch, "E452", {"start": v(-1.32, -12.9) * mm, "end": v(1.85, -12.9) * mm});
            skPoint(sketch, "E453.visualSharp", {"position": v(-2.26, -12.9) * mm});
            skArc(sketch, "E453.filletArc", {"start": v(-3.03, -12.37) * mm, "mid": v(-2.22, -12.77) * mm, "end": v(-1.32, -12.9) * mm});
            skPoint(sketch, "E454.visualSharp", {"position": v(7.05, -12.9) * mm});
            skLineSegment(sketch, "E455", {"start": v(2.45, -4.94) * mm, "end": v(4.45, -8.4) * mm});
            skArc(sketch, "E456.filletArc", {"start": v(1.85, -12.9) * mm, "mid": v(4.45, -11.4) * mm, "end": v(4.45, -8.4) * mm});
            skSolve(sketch);
        }
        {
            var Q0;
            Q0=qCreatedBy(makeId("Top.planeOp"),FACE);
            var sketch = newSketch(context, id + "F32", { "sketchPlane" : qUnion([Q0])});
            skLineSegment(sketch, "E457.bottom", {"start": v(44.97, -1.8) * mm, "end": v(-21.03, -1.8) * mm});
            skLineSegment(sketch, "E457.top", {"start": v(44.97, 36.2) * mm, "end": v(-21.03, 36.2) * mm});
            skLineSegment(sketch, "E457.left", {"start": v(44.97, -1.8) * mm, "end": v(44.97, 36.2) * mm});
            skLineSegment(sketch, "E457.right", {"start": v(-21.03, -1.8) * mm, "end": v(-21.03, 36.2) * mm});
            skPoint(sketch, "E457.middle", {"position": v(11.97, 17.2) * mm});
            skSolve(sketch);
        }
        {
            var Q0;
            Q0 = qSketchRegion(id + "F32", true);
            extrude(context, id + "F33", {"entities" : qUnion([Q0]), "depth" : 21 * mm});
        }
        {
            var Q0;
            Q0 = qSketchRegion(id + "F31", true);
            extrude(context, id + "F34", {"entities" : qUnion([Q0]), "depth" : 2 * mm});
        }
        {
            var Q0;
            Q0=qCreatedBy(makeId("Top.planeOp"),FACE);
            var sketch = newSketch(context, id + "F35", { "sketchPlane" : qUnion([Q0])});
            skLineSegment(sketch, "E458.bottom", {"start": v(20.95, -17.63) * mm, "end": v(-19.05, -17.63) * mm});
            skLineSegment(sketch, "E458.top", {"start": v(20.95, 22.37) * mm, "end": v(-19.05, 22.37) * mm});
            skPoint(sketch, "E458.middle", {"position": v(0.95, 2.37) * mm});
            skLineSegment(sketch, "E459.bottom", {"start": v(14.95, -11.63) * mm, "end": v(-13.05, -11.63) * mm, "construction": true});
            skLineSegment(sketch, "E459.top", {"start": v(14.95, 16.37) * mm, "end": v(-13.05, 16.37) * mm, "construction": true});
            skLineSegment(sketch, "E459.left", {"start": v(14.95, -11.63) * mm, "end": v(14.95, 16.37) * mm, "construction": true});
            skLineSegment(sketch, "E459.right", {"start": v(-13.05, -11.63) * mm, "end": v(-13.05, 16.37) * mm, "construction": true});
            skCircle(sketch, "E460", {"center": v(14.95, 16.37) * mm, "radius": 1 * mm});
            skCircle(sketch, "E461", {"center": v(-13.05, 16.37) * mm, "radius": 1 * mm});
            skCircle(sketch, "E462", {"center": v(14.95, -11.63) * mm, "radius": 1 * mm});
            skCircle(sketch, "E463", {"center": v(-13.05, -11.63) * mm, "radius": 1 * mm});
            skCircle(sketch, "E464", {"center": v(0.95, 2.37) * mm, "radius": 12.5 * mm});
            skLineSegment(sketch, "E465", {"start": v(-19.05, 22.37) * mm, "end": v(-21.05, 22.37) * mm});
            skLineSegment(sketch, "E466", {"start": v(-21.05, 22.37) * mm, "end": v(-21.05, 12.37) * mm});
            skLineSegment(sketch, "E467", {"start": v(-21.05, 12.37) * mm, "end": v(-19.05, 12.37) * mm});
            skLineSegment(sketch, "E468", {"start": v(-19.05, 12.37) * mm, "end": v(-19.05, 2.37) * mm});
            skLineSegment(sketch, "E469", {"start": v(-19.05, 2.37) * mm, "end": v(-21.05, 2.37) * mm});
            skLineSegment(sketch, "E470", {"start": v(-21.05, 2.37) * mm, "end": v(-21.05, -7.63) * mm});
            skLineSegment(sketch, "E471", {"start": v(-21.05, -7.63) * mm, "end": v(-19.05, -7.63) * mm});
            skLineSegment(sketch, "E472", {"start": v(-19.05, -7.63) * mm, "end": v(-19.05, -17.63) * mm});
            skLineSegment(sketch, "E473", {"start": v(0.95, 2.37) * mm, "end": v(0.95, 9.24) * mm});
            skLineSegment(sketch, "E474.MirrorCS", {"start": v(20.95, 22.37) * mm, "end": v(22.95, 22.37) * mm});
            skLineSegment(sketch, "E475.MirrorCS", {"start": v(20.95, 2.37) * mm, "end": v(22.95, 2.37) * mm});
            skLineSegment(sketch, "E476.MirrorCS", {"start": v(20.95, 12.37) * mm, "end": v(20.95, 2.37) * mm});
            skLineSegment(sketch, "E477.MirrorCS", {"start": v(22.95, 2.37) * mm, "end": v(22.95, -7.63) * mm});
            skLineSegment(sketch, "E478.MirrorCS", {"start": v(22.95, 22.37) * mm, "end": v(22.95, 12.37) * mm});
            skLineSegment(sketch, "E479.MirrorCS", {"start": v(22.95, 12.37) * mm, "end": v(20.95, 12.37) * mm});
            skLineSegment(sketch, "E480.MirrorCS", {"start": v(20.95, -7.63) * mm, "end": v(20.95, -17.63) * mm});
            skLineSegment(sketch, "E481.MirrorCS", {"start": v(22.95, -7.63) * mm, "end": v(20.95, -7.63) * mm});
            skSolve(sketch);
        }
        {
            var Q0;
            Q0 = qSketchRegion(id + "F35", true);
            extrude(context, id + "F36", {"entities" : qUnion([Q0]), "depth" : 2 * mm});
        }
    });
